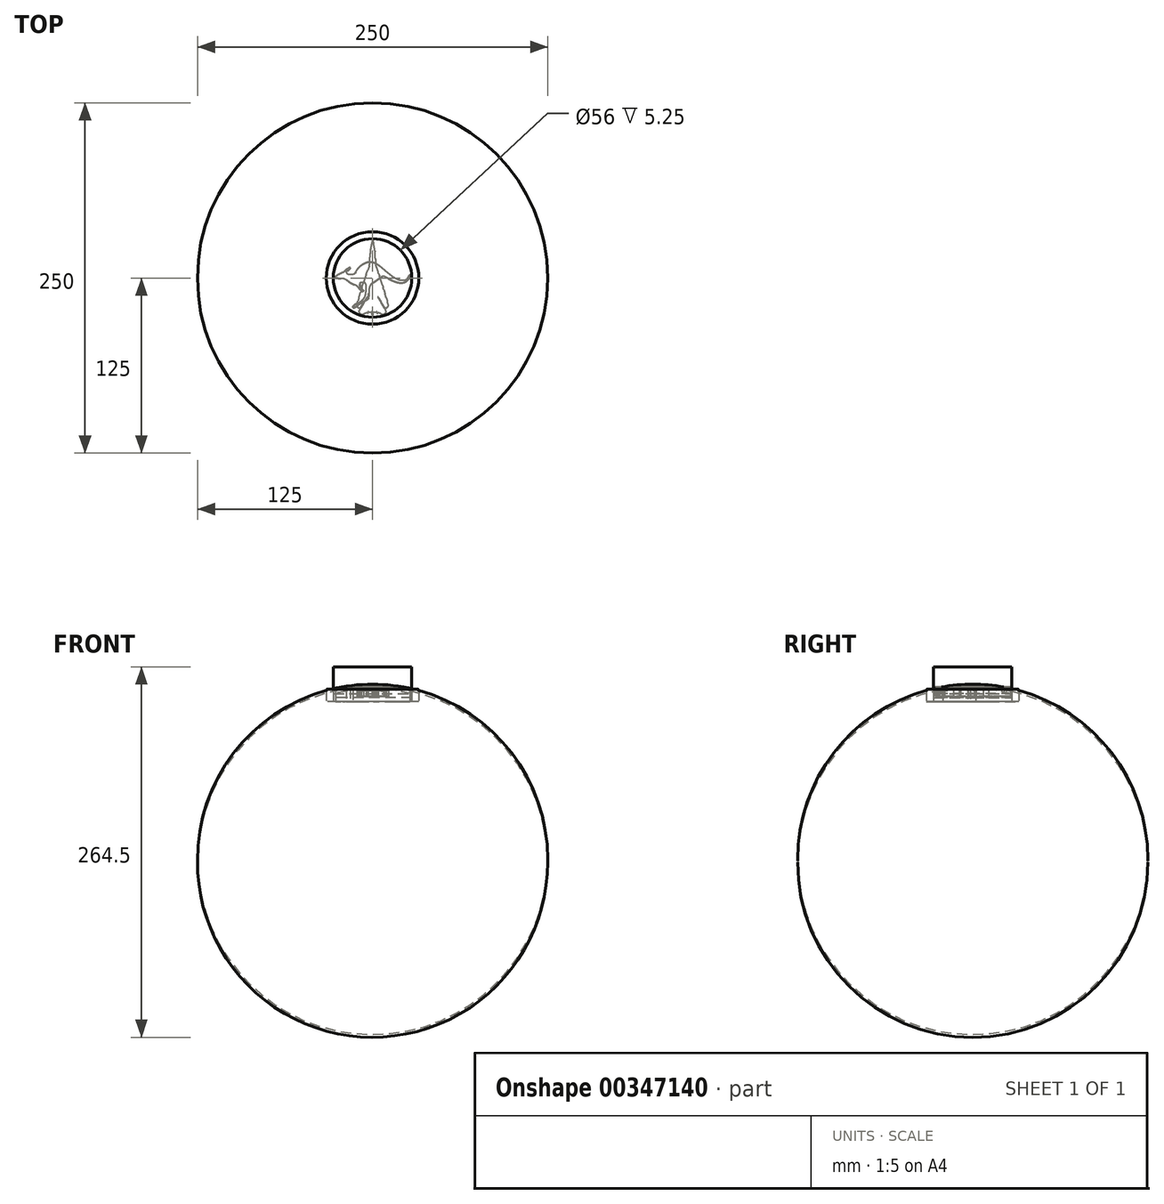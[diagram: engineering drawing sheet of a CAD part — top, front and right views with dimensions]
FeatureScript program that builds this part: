
annotation { "Feature Type Name" : "Feature", "Feature Type Description" : "" }
export const myFeature = defineFeature(function(context is Context, id is Id, definition is map)
    precondition{}
    {
        {
            var Q0;
            Q0=qCreatedBy(makeId("Top.planeOp"),FACE);
            var sketch = newSketch(context, id + "F0", { "sketchPlane" : qUnion([Q0])});
            skCircle(sketch, "E0", {"center": v(0, 0) * mm, "radius": 33 * mm});
            skSolve(sketch);
        }
        {
            var Q0;
            Q0 = qSketchRegion(id + "F0", true);
            extrude(context, id + "F1", {"entities" : qUnion([Q0]), "depth" : 3 * mm});
        }
        {
            var Q0;
            Q0=qCreatedBy(makeId("Top.planeOp"),FACE);
            var sketch = newSketch(context, id + "F2", { "sketchPlane" : qUnion([Q0])});
            skCircle(sketch, "E1", {"center": v(0, 0) * mm, "radius": 33 * mm});
            skCircle(sketch, "E2", {"center": v(0, 0) * mm, "radius": 28 * mm});
            skSolve(sketch);
        }
        {
            var Q0;
            Q0 = qSketchRegion(id + "F2", true);
            extrude(context, id + "F3", {"entities" : qUnion([Q0]), "operationType" : NewBodyOperationType.ADD, "depth" : 9 * mm});
        }
        {
            var Q0;
            Q0=makeQuery(id+"F3.opExtrude","CAP_EDGE",EDGE,{"disambiguationData":[OSD([sQuery(id+"F2.wireOp",EDGE,"E1")])],"isStart":false});
            var Q1;
            Q1=makeQuery(id+"F3.opExtrude","CAP_EDGE",EDGE,{"disambiguationData":[OSD([sQuery(id+"F2.wireOp",EDGE,"E2")])],"isStart":false});
            fillet(context, id + "F4", {"entities" : qUnion([Q0, Q1]), "radius" : 0.75 * mm, "tangentPropagation" : true, "allowEdgeOverflow" : false});
        }
        {
            var Q0;
            Q0=qCreatedBy(makeId("Top.planeOp"),FACE);
            var sketch = newSketch(context, id + "F5", { "sketchPlane" : qUnion([Q0])});
            skArc(sketch, "E3", {"start": v(0, 125) * mm, "mid": v(-125, 0) * mm, "end": v(0, -125) * mm});
            skLineSegment(sketch, "E4", {"start": v(0, 0) * mm, "end": v(0, 125) * mm});
            skLineSegment(sketch, "E5", {"start": v(0, 0) * mm, "end": v(0, -125) * mm});
            skSolve(sketch);
        }
        {
            var Q0;
            Q0=makeQuery(id+"F5.imprint","IMPRINT",FACE,{"disambiguationData":[TD([[makeQuery(id+"F5.imprint","IMPRINT",EDGE,{"derivedFrom":sQuery(id+"F5.wireOp",EDGE,"E3")}),1.0]])]});
            var Q1;
            Q1=sQuery(id+"F5.wireOp",EDGE,"E4");
            revolve(context, id + "F6", {"entities" : qUnion([Q0]), "axis" : qUnion([Q1]), "revolveType" : RevolveType.FULL});
        }
        {
            var Q0;
            Q0=makeQuery(id+"F6.opRevolve","SWEPT_BODY",BODY,{"disambiguationData":[OSD([sQuery(id+"F5.wireOp",EDGE,"E3"),sQuery(id+"F5.wireOp",EDGE,"E4"),sQuery(id+"F5.wireOp",EDGE,"E5")])]});
            transform(context, id + "F7", {"entities" : qUnion([Q0]), "transformType" : TransformType.TRANSLATION_3D, "dx" : 0 * mm, "dy" : 0 * mm, "dz" : -112.5 * mm, "makeCopy" : false});
        }
        {
            var Q0;
            Q0=qCreatedBy(makeId("Top.planeOp"),FACE);
            var sketch = newSketch(context, id + "F8", { "sketchPlane" : qUnion([Q0])});
            skArc(sketch, "E6", {"start": v(-1.06, 204.98) * mm, "mid": v(-3.06, 197.7) * mm, "end": v(-4.96, 190.37) * mm});
            skArc(sketch, "E7", {"start": v(-4.96, 190.37) * mm, "mid": v(-6.57, 183.77) * mm, "end": v(-8.05, 177.14) * mm});
            skArc(sketch, "E8", {"start": v(-8.05, 177.14) * mm, "mid": v(-9.38, 170.65) * mm, "end": v(-10.58, 164.14) * mm});
            skArc(sketch, "E9", {"start": v(-10.58, 164.14) * mm, "mid": v(-11.75, 157.2) * mm, "end": v(-12.8, 150.23) * mm});
            skArc(sketch, "E10", {"start": v(-12.8, 150.23) * mm, "mid": v(-13.03, 148.33) * mm, "end": v(-13.2, 146.42) * mm});
            skArc(sketch, "E11", {"start": v(-13.2, 146.42) * mm, "mid": v(-13.47, 141.8) * mm, "end": v(-13.73, 137.18) * mm});
            skArc(sketch, "E12", {"start": v(-13.73, 137.18) * mm, "mid": v(-14.01, 131.67) * mm, "end": v(-14.27, 126.16) * mm});
            skArc(sketch, "E13", {"start": v(-14.27, 126.16) * mm, "mid": v(-14.52, 120.2) * mm, "end": v(-14.75, 114.23) * mm});
            skArc(sketch, "E14", {"start": v(-14.75, 114.23) * mm, "mid": v(-14.97, 108.2) * mm, "end": v(-15.2, 102.16) * mm});
            skArc(sketch, "E15", {"start": v(-15.2, 102.16) * mm, "mid": v(-15.4, 96.43) * mm, "end": v(-15.62, 90.7) * mm});
            skArc(sketch, "E16", {"start": v(-15.62, 90.7) * mm, "mid": v(-15.8, 85.85) * mm, "end": v(-15.98, 81) * mm});
            skArc(sketch, "E17", {"start": v(-15.98, 81) * mm, "mid": v(-16.08, 78.62) * mm, "end": v(-16.17, 76.23) * mm});
            skArc(sketch, "E18", {"start": v(-16.17, 76.23) * mm, "mid": v(-16.27, 74.54) * mm, "end": v(-16.41, 72.86) * mm});
            skArc(sketch, "E19", {"start": v(-16.41, 72.86) * mm, "mid": v(-16.61, 71.19) * mm, "end": v(-16.86, 69.53) * mm});
            skArc(sketch, "E20", {"start": v(-16.86, 69.53) * mm, "mid": v(-17.13, 68.08) * mm, "end": v(-17.45, 66.63) * mm});
            skArc(sketch, "E21", {"start": v(-17.45, 66.63) * mm, "mid": v(-17.73, 65.67) * mm, "end": v(-18.1, 64.73) * mm});
            skArc(sketch, "E22", {"start": v(-18.1, 64.73) * mm, "mid": v(-18.6, 63.61) * mm, "end": v(-19.05, 62.47) * mm});
            skArc(sketch, "E23", {"start": v(-19.05, 62.47) * mm, "mid": v(-20.12, 59.65) * mm, "end": v(-21.18, 56.83) * mm});
            skArc(sketch, "E24", {"start": v(-21.18, 56.83) * mm, "mid": v(-22.43, 53.45) * mm, "end": v(-23.67, 50.07) * mm});
            skArc(sketch, "E25", {"start": v(-23.67, 50.07) * mm, "mid": v(-25, 46.4) * mm, "end": v(-26.32, 42.73) * mm});
            skArc(sketch, "E26", {"start": v(-26.32, 42.73) * mm, "mid": v(-27.66, 39) * mm, "end": v(-29, 35.28) * mm});
            skArc(sketch, "E27", {"start": v(-29, 35.28) * mm, "mid": v(-30.27, 31.74) * mm, "end": v(-31.55, 28.2) * mm});
            skArc(sketch, "E28", {"start": v(-31.55, 28.2) * mm, "mid": v(-32.63, 25.2) * mm, "end": v(-33.72, 22.2) * mm});
            skArc(sketch, "E29", {"start": v(-33.72, 22.2) * mm, "mid": v(-34.26, 20.72) * mm, "end": v(-34.81, 19.23) * mm});
            skArc(sketch, "E30", {"start": v(-34.81, 19.23) * mm, "mid": v(-37.05, 13.14) * mm, "end": v(-39.24, 7.03) * mm});
            skArc(sketch, "E31", {"start": v(-39.24, 7.03) * mm, "mid": v(-41.5, 0.56) * mm, "end": v(-43.7, -5.92) * mm});
            skArc(sketch, "E32", {"start": v(-43.7, -5.92) * mm, "mid": v(-45.8, -12.23) * mm, "end": v(-47.85, -18.55) * mm});
            skArc(sketch, "E33", {"start": v(-47.85, -18.55) * mm, "mid": v(-49.62, -24.15) * mm, "end": v(-51.32, -29.77) * mm});
            skArc(sketch, "E34", {"start": v(-51.32, -29.77) * mm, "mid": v(-52.3, -33.05) * mm, "end": v(-53.27, -36.33) * mm});
            skArc(sketch, "E35", {"start": v(-53.27, -36.33) * mm, "mid": v(-54.25, -39.58) * mm, "end": v(-55.22, -42.83) * mm});
            skArc(sketch, "E36", {"start": v(-55.22, -42.83) * mm, "mid": v(-56.06, -45.64) * mm, "end": v(-56.91, -48.46) * mm});
            skArc(sketch, "E37", {"start": v(-56.91, -48.46) * mm, "mid": v(-57.41, -50.11) * mm, "end": v(-57.92, -51.77) * mm});
            skArc(sketch, "E38", {"start": v(-57.92, -51.77) * mm, "mid": v(-58.46, -53.54) * mm, "end": v(-59, -55.32) * mm});
            skArc(sketch, "E39", {"start": v(-59, -55.32) * mm, "mid": v(-60.07, -58.9) * mm, "end": v(-61.14, -62.47) * mm});
            skArc(sketch, "E40", {"start": v(-61.14, -62.47) * mm, "mid": v(-62.4, -66.69) * mm, "end": v(-63.66, -70.9) * mm});
            skArc(sketch, "E41", {"start": v(-63.66, -70.9) * mm, "mid": v(-64.98, -75.34) * mm, "end": v(-66.3, -79.77) * mm});
            skArc(sketch, "E42", {"start": v(-66.3, -79.77) * mm, "mid": v(-67.61, -84.2) * mm, "end": v(-68.93, -88.63) * mm});
            skArc(sketch, "E43", {"start": v(-68.93, -88.63) * mm, "mid": v(-70.2, -92.85) * mm, "end": v(-71.46, -97.07) * mm});
            skArc(sketch, "E44", {"start": v(-71.46, -97.07) * mm, "mid": v(-72.54, -100.64) * mm, "end": v(-73.62, -104.2) * mm});
            skArc(sketch, "E45", {"start": v(-73.62, -104.2) * mm, "mid": v(-74.16, -105.99) * mm, "end": v(-74.72, -107.77) * mm});
            skArc(sketch, "E46", {"start": v(-74.72, -107.77) * mm, "mid": v(-75.2, -109.29) * mm, "end": v(-75.66, -110.82) * mm});
            skArc(sketch, "E47", {"start": v(-75.66, -110.82) * mm, "mid": v(-76.33, -113.03) * mm, "end": v(-76.99, -115.24) * mm});
            skArc(sketch, "E48", {"start": v(-76.99, -115.24) * mm, "mid": v(-77.71, -117.67) * mm, "end": v(-78.43, -120.12) * mm});
            skArc(sketch, "E49", {"start": v(-78.43, -120.12) * mm, "mid": v(-79.11, -122.44) * mm, "end": v(-79.79, -124.77) * mm});
            skArc(sketch, "E50", {"start": v(-79.79, -124.77) * mm, "mid": v(-80.44, -127.01) * mm, "end": v(-81.11, -129.26) * mm});
            skArc(sketch, "E51", {"start": v(-81.11, -129.26) * mm, "mid": v(-81.78, -131.46) * mm, "end": v(-82.46, -133.66) * mm});
            skArc(sketch, "E52", {"start": v(-82.46, -133.66) * mm, "mid": v(-83.05, -135.55) * mm, "end": v(-83.66, -137.44) * mm});
            skArc(sketch, "E53", {"start": v(-83.66, -137.44) * mm, "mid": v(-84.02, -138.52) * mm, "end": v(-84.4, -139.6) * mm});
            skArc(sketch, "E54", {"start": v(-84.4, -139.6) * mm, "mid": v(-84.73, -140.52) * mm, "end": v(-85, -141.46) * mm});
            skArc(sketch, "E55", {"start": v(-85, -141.46) * mm, "mid": v(-85.32, -142.71) * mm, "end": v(-85.6, -143.97) * mm});
            skArc(sketch, "E56", {"start": v(-85.6, -143.97) * mm, "mid": v(-85.87, -145.3) * mm, "end": v(-86.11, -146.65) * mm});
            skArc(sketch, "E57", {"start": v(-86.11, -146.65) * mm, "mid": v(-86.3, -147.88) * mm, "end": v(-86.44, -149.11) * mm});
            skLineSegment(sketch, "E58", {"start": v(-86.44, -149.11) * mm, "end": v(-87.04, -154.8) * mm});
            skLineSegment(sketch, "E59", {"start": v(-87.04, -154.8) * mm, "end": v(-82.61, -158.78) * mm});
            skArc(sketch, "E60", {"start": v(-82.61, -158.78) * mm, "mid": v(-80.32, -160.83) * mm, "end": v(-78.01, -162.85) * mm});
            skArc(sketch, "E61", {"start": v(-78.01, -162.85) * mm, "mid": v(-76.6, -164.03) * mm, "end": v(-75.15, -165.16) * mm});
            skArc(sketch, "E62", {"start": v(-75.15, -165.16) * mm, "mid": v(-74.15, -165.86) * mm, "end": v(-73.12, -166.5) * mm});
            skArc(sketch, "E63", {"start": v(-73.12, -166.5) * mm, "mid": v(-72.35, -166.85) * mm, "end": v(-71.54, -167.06) * mm});
            skArc(sketch, "E64", {"start": v(-71.54, -167.06) * mm, "mid": v(-70.52, -166.96) * mm, "end": v(-69.69, -166.35) * mm});
            skArc(sketch, "E65", {"start": v(-69.69, -166.35) * mm, "mid": v(-67.91, -164.03) * mm, "end": v(-66.22, -161.65) * mm});
            skArc(sketch, "E66", {"start": v(-66.22, -161.65) * mm, "mid": v(-63.23, -157.17) * mm, "end": v(-60.33, -152.63) * mm});
            skArc(sketch, "E67", {"start": v(-60.33, -152.63) * mm, "mid": v(-52.8, -140.6) * mm, "end": v(-45.3, -128.56) * mm});
            skArc(sketch, "E68", {"start": v(-45.3, -128.56) * mm, "mid": v(-42.19, -123.59) * mm, "end": v(-39.04, -118.63) * mm});
            skArc(sketch, "E69", {"start": v(-39.04, -118.63) * mm, "mid": v(-36.68, -115.01) * mm, "end": v(-34.26, -111.43) * mm});
            skArc(sketch, "E70", {"start": v(-34.26, -111.43) * mm, "mid": v(-32.42, -108.78) * mm, "end": v(-30.55, -106.14) * mm});
            skArc(sketch, "E71", {"start": v(-30.55, -106.14) * mm, "mid": v(-30.23, -106.02) * mm, "end": v(-30, -106.27) * mm});
            skArc(sketch, "E72", {"start": v(-30, -106.27) * mm, "mid": v(-30, -106.96) * mm, "end": v(-30.23, -107.61) * mm});
            skArc(sketch, "E73", {"start": v(-30.23, -107.61) * mm, "mid": v(-32.67, -111.88) * mm, "end": v(-35.13, -116.13) * mm});
            skArc(sketch, "E74", {"start": v(-35.13, -116.13) * mm, "mid": v(-38.05, -121.11) * mm, "end": v(-41.03, -126.07) * mm});
            skArc(sketch, "E75", {"start": v(-41.03, -126.07) * mm, "mid": v(-44.62, -131.93) * mm, "end": v(-48.24, -137.77) * mm});
            skArc(sketch, "E76", {"start": v(-48.24, -137.77) * mm, "mid": v(-51.81, -143.5) * mm, "end": v(-55.36, -149.25) * mm});
            skArc(sketch, "E77", {"start": v(-55.36, -149.25) * mm, "mid": v(-58.37, -154.2) * mm, "end": v(-61.35, -159.16) * mm});
            skArc(sketch, "E78", {"start": v(-61.35, -159.16) * mm, "mid": v(-63.93, -163.5) * mm, "end": v(-66.5, -167.85) * mm});
            skArc(sketch, "E79", {"start": v(-66.5, -167.85) * mm, "mid": v(-66.73, -168.37) * mm, "end": v(-66.8, -168.92) * mm});
            skArc(sketch, "E80", {"start": v(-66.8, -168.92) * mm, "mid": v(-66.85, -169.34) * mm, "end": v(-66.97, -169.75) * mm});
            skArc(sketch, "E81", {"start": v(-66.97, -169.75) * mm, "mid": v(-67.32, -170.5) * mm, "end": v(-67.68, -171.25) * mm});
            skArc(sketch, "E82", {"start": v(-67.68, -171.25) * mm, "mid": v(-68.15, -172.13) * mm, "end": v(-68.65, -172.99) * mm});
            skArc(sketch, "E83", {"start": v(-68.65, -172.99) * mm, "mid": v(-69.22, -173.89) * mm, "end": v(-69.8, -174.77) * mm});
            skArc(sketch, "E84", {"start": v(-69.8, -174.77) * mm, "mid": v(-70.39, -175.63) * mm, "end": v(-70.95, -176.5) * mm});
            skArc(sketch, "E85", {"start": v(-70.95, -176.5) * mm, "mid": v(-71.45, -177.3) * mm, "end": v(-71.92, -178.12) * mm});
            skArc(sketch, "E86", {"start": v(-71.92, -178.12) * mm, "mid": v(-72.3, -178.8) * mm, "end": v(-72.66, -179.5) * mm});
            skArc(sketch, "E87", {"start": v(-72.66, -179.5) * mm, "mid": v(-72.77, -179.78) * mm, "end": v(-72.8, -180.07) * mm});
            skArc(sketch, "E88", {"start": v(-72.8, -180.07) * mm, "mid": v(-72.83, -180.3) * mm, "end": v(-72.9, -180.52) * mm});
            skArc(sketch, "E89", {"start": v(-72.9, -180.52) * mm, "mid": v(-73.06, -180.82) * mm, "end": v(-73.24, -181.1) * mm});
            skArc(sketch, "E90", {"start": v(-73.24, -181.1) * mm, "mid": v(-73.47, -181.42) * mm, "end": v(-73.73, -181.72) * mm});
            skArc(sketch, "E91", {"start": v(-73.73, -181.72) * mm, "mid": v(-74, -182) * mm, "end": v(-74.3, -182.27) * mm});
            skArc(sketch, "E92", {"start": v(-74.3, -182.27) * mm, "mid": v(-75.1, -183.2) * mm, "end": v(-75.57, -184.33) * mm});
            skArc(sketch, "E93", {"start": v(-75.57, -184.33) * mm, "mid": v(-75.65, -185.57) * mm, "end": v(-75.33, -186.77) * mm});
            skArc(sketch, "E94", {"start": v(-75.33, -186.77) * mm, "mid": v(-74.44, -188.46) * mm, "end": v(-73.29, -190) * mm});
            skArc(sketch, "E95", {"start": v(-73.29, -190) * mm, "mid": v(-71.11, -192.4) * mm, "end": v(-68.86, -194.71) * mm});
            skLineSegment(sketch, "E96", {"start": v(-68.86, -194.71) * mm, "end": v(-61.91, -201.6) * mm});
            skLineSegment(sketch, "E97", {"start": v(-61.91, -201.6) * mm, "end": v(-45.75, -196.22) * mm});
            skArc(sketch, "E98", {"start": v(-45.75, -196.22) * mm, "mid": v(-40.84, -194.6) * mm, "end": v(-35.92, -193) * mm});
            skArc(sketch, "E99", {"start": v(-35.92, -193) * mm, "mid": v(-33.9, -192.4) * mm, "end": v(-31.87, -191.92) * mm});
            skArc(sketch, "E100", {"start": v(-31.87, -191.92) * mm, "mid": v(-30.77, -191.77) * mm, "end": v(-29.66, -191.8) * mm});
            skArc(sketch, "E101", {"start": v(-29.66, -191.8) * mm, "mid": v(-28.92, -192.03) * mm, "end": v(-28.34, -192.55) * mm});
            skArc(sketch, "E102", {"start": v(-28.34, -192.55) * mm, "mid": v(-28.05, -192.9) * mm, "end": v(-27.73, -193.2) * mm});
            skArc(sketch, "E103", {"start": v(-27.73, -193.2) * mm, "mid": v(-27.36, -193.5) * mm, "end": v(-26.95, -193.76) * mm});
            skArc(sketch, "E104", {"start": v(-26.95, -193.76) * mm, "mid": v(-26.55, -193.97) * mm, "end": v(-26.13, -194.14) * mm});
            skArc(sketch, "E105", {"start": v(-26.13, -194.14) * mm, "mid": v(-25.77, -194.24) * mm, "end": v(-25.4, -194.27) * mm});
            skArc(sketch, "E106", {"start": v(-25.4, -194.27) * mm, "mid": v(-24.96, -194.2) * mm, "end": v(-24.56, -194) * mm});
            skArc(sketch, "E107", {"start": v(-24.56, -194) * mm, "mid": v(-24.26, -193.7) * mm, "end": v(-24.07, -193.31) * mm});
            skArc(sketch, "E108", {"start": v(-24.07, -193.31) * mm, "mid": v(-23.92, -192.63) * mm, "end": v(-23.87, -191.94) * mm});
            skArc(sketch, "E109", {"start": v(-23.87, -191.94) * mm, "mid": v(-23.89, -190.61) * mm, "end": v(-23.93, -189.28) * mm});
            skArc(sketch, "E110", {"start": v(-23.93, -189.28) * mm, "mid": v(-23.97, -187.55) * mm, "end": v(-23.94, -185.82) * mm});
            skArc(sketch, "E111", {"start": v(-23.94, -185.82) * mm, "mid": v(-23.8, -184.8) * mm, "end": v(-23.49, -183.8) * mm});
            skArc(sketch, "E112", {"start": v(-23.49, -183.8) * mm, "mid": v(-23.19, -183.57) * mm, "end": v(-22.83, -183.7) * mm});
            skArc(sketch, "E113", {"start": v(-22.83, -183.7) * mm, "mid": v(-22.42, -184.35) * mm, "end": v(-22.15, -185.06) * mm});
            skArc(sketch, "E114", {"start": v(-22.15, -185.06) * mm, "mid": v(-21.9, -185.7) * mm, "end": v(-21.51, -186.27) * mm});
            skArc(sketch, "E115", {"start": v(-21.51, -186.27) * mm, "mid": v(-21.04, -186.68) * mm, "end": v(-20.46, -186.93) * mm});
            skArc(sketch, "E116", {"start": v(-20.46, -186.93) * mm, "mid": v(-19.48, -187.13) * mm, "end": v(-18.48, -187.2) * mm});
            skArc(sketch, "E117", {"start": v(-18.48, -187.2) * mm, "mid": v(-16.14, -187.25) * mm, "end": v(-13.8, -187.27) * mm});
            skArc(sketch, "E118", {"start": v(-13.8, -187.27) * mm, "mid": v(-11.45, -187.25) * mm, "end": v(-9.1, -187.2) * mm});
            skArc(sketch, "E119", {"start": v(-9.1, -187.2) * mm, "mid": v(-8.1, -187.13) * mm, "end": v(-7.13, -186.93) * mm});
            skArc(sketch, "E120", {"start": v(-7.13, -186.93) * mm, "mid": v(-6.56, -186.68) * mm, "end": v(-6.09, -186.26) * mm});
            skArc(sketch, "E121", {"start": v(-6.09, -186.26) * mm, "mid": v(-5.7, -185.68) * mm, "end": v(-5.45, -185.03) * mm});
            skArc(sketch, "E122", {"start": v(-5.45, -185.03) * mm, "mid": v(-5.13, -184.33) * mm, "end": v(-4.58, -183.77) * mm});
            skArc(sketch, "E123", {"start": v(-4.58, -183.77) * mm, "mid": v(-4.06, -183.67) * mm, "end": v(-3.66, -184) * mm});
            skArc(sketch, "E124", {"start": v(-3.66, -184) * mm, "mid": v(-3.2, -185.24) * mm, "end": v(-2.97, -186.54) * mm});
            skArc(sketch, "E125", {"start": v(-2.97, -186.54) * mm, "mid": v(-2.9, -188.35) * mm, "end": v(-2.95, -190.17) * mm});
            skArc(sketch, "E126", {"start": v(-2.95, -190.17) * mm, "mid": v(-3, -191.15) * mm, "end": v(-3.03, -192.13) * mm});
            skArc(sketch, "E127", {"start": v(-3.03, -192.13) * mm, "mid": v(-3.02, -192.95) * mm, "end": v(-2.98, -193.77) * mm});
            skArc(sketch, "E128", {"start": v(-2.98, -193.77) * mm, "mid": v(-2.92, -194.4) * mm, "end": v(-2.83, -195.03) * mm});
            skArc(sketch, "E129", {"start": v(-2.83, -195.03) * mm, "mid": v(-2.74, -195.2) * mm, "end": v(-2.55, -195.27) * mm});
            skArc(sketch, "E130", {"start": v(-2.55, -195.27) * mm, "mid": v(-2.36, -195.34) * mm, "end": v(-2.26, -195.5) * mm});
            skArc(sketch, "E131", {"start": v(-2.26, -195.5) * mm, "mid": v(-2.13, -196.18) * mm, "end": v(-2.02, -196.87) * mm});
            skArc(sketch, "E132", {"start": v(-2.02, -196.87) * mm, "mid": v(-1.92, -197.74) * mm, "end": v(-1.86, -198.62) * mm});
            skArc(sketch, "E133", {"start": v(-1.86, -198.62) * mm, "mid": v(-1.82, -199.66) * mm, "end": v(-1.8, -200.7) * mm});
            skArc(sketch, "E134", {"start": v(-1.8, -200.7) * mm, "mid": v(-1.76, -202.46) * mm, "end": v(-1.64, -204.2) * mm});
            skArc(sketch, "E135", {"start": v(-1.64, -204.2) * mm, "mid": v(-1.43, -205.28) * mm, "end": v(-1.04, -206.3) * mm});
            skArc(sketch, "E136", {"start": v(-1.04, -206.3) * mm, "mid": v(-0.68, -206.67) * mm, "end": v(-0.17, -206.74) * mm});
            skArc(sketch, "E137", {"start": v(-0.17, -206.74) * mm, "mid": v(0.4, -206.51) * mm, "end": v(0.82, -206.07) * mm});
            skArc(sketch, "E138", {"start": v(0.82, -206.07) * mm, "mid": v(1, -205.72) * mm, "end": v(1.1, -205.34) * mm});
            skArc(sketch, "E139", {"start": v(1.1, -205.34) * mm, "mid": v(1.2, -204.66) * mm, "end": v(1.28, -203.98) * mm});
            skArc(sketch, "E140", {"start": v(1.28, -203.98) * mm, "mid": v(1.33, -203.17) * mm, "end": v(1.36, -202.35) * mm});
            skArc(sketch, "E141", {"start": v(1.36, -202.35) * mm, "mid": v(1.35, -201.5) * mm, "end": v(1.32, -200.66) * mm});
            skArc(sketch, "E142", {"start": v(1.32, -200.66) * mm, "mid": v(1.29, -199.83) * mm, "end": v(1.3, -199) * mm});
            skArc(sketch, "E143", {"start": v(1.3, -199) * mm, "mid": v(1.35, -198.25) * mm, "end": v(1.45, -197.5) * mm});
            skArc(sketch, "E144", {"start": v(1.45, -197.5) * mm, "mid": v(1.57, -196.91) * mm, "end": v(1.73, -196.32) * mm});
            skArc(sketch, "E145", {"start": v(1.73, -196.32) * mm, "mid": v(1.88, -196.03) * mm, "end": v(2.13, -195.8) * mm});
            skArc(sketch, "E146", {"start": v(2.13, -195.8) * mm, "mid": v(2.39, -195.57) * mm, "end": v(2.55, -195.25) * mm});
            skArc(sketch, "E147", {"start": v(2.55, -195.25) * mm, "mid": v(2.73, -194.5) * mm, "end": v(2.88, -193.74) * mm});
            skArc(sketch, "E148", {"start": v(2.88, -193.74) * mm, "mid": v(3.03, -192.8) * mm, "end": v(3.12, -191.84) * mm});
            skArc(sketch, "E149", {"start": v(3.12, -191.84) * mm, "mid": v(3.18, -190.77) * mm, "end": v(3.2, -189.7) * mm});
            skArc(sketch, "E150", {"start": v(3.2, -189.7) * mm, "mid": v(3.22, -188.66) * mm, "end": v(3.27, -187.62) * mm});
            skArc(sketch, "E151", {"start": v(3.27, -187.62) * mm, "mid": v(3.36, -186.74) * mm, "end": v(3.5, -185.87) * mm});
            skArc(sketch, "E152", {"start": v(3.5, -185.87) * mm, "mid": v(3.63, -185.2) * mm, "end": v(3.8, -184.56) * mm});
            skArc(sketch, "E153", {"start": v(3.8, -184.56) * mm, "mid": v(3.95, -184.35) * mm, "end": v(4.2, -184.27) * mm});
            skArc(sketch, "E154", {"start": v(4.2, -184.27) * mm, "mid": v(4.4, -184.3) * mm, "end": v(4.58, -184.38) * mm});
            skArc(sketch, "E155", {"start": v(4.58, -184.38) * mm, "mid": v(4.76, -184.53) * mm, "end": v(4.9, -184.7) * mm});
            skArc(sketch, "E156", {"start": v(4.9, -184.7) * mm, "mid": v(5.03, -184.94) * mm, "end": v(5.12, -185.2) * mm});
            skArc(sketch, "E157", {"start": v(5.12, -185.2) * mm, "mid": v(5.18, -185.48) * mm, "end": v(5.2, -185.77) * mm});
            skArc(sketch, "E158", {"start": v(5.2, -185.77) * mm, "mid": v(5.31, -186.2) * mm, "end": v(5.63, -186.52) * mm});
            skArc(sketch, "E159", {"start": v(5.63, -186.52) * mm, "mid": v(6.23, -186.8) * mm, "end": v(6.86, -186.97) * mm});
            skArc(sketch, "E160", {"start": v(6.86, -186.97) * mm, "mid": v(8.04, -187.13) * mm, "end": v(9.22, -187.2) * mm});
            skArc(sketch, "E161", {"start": v(9.22, -187.2) * mm, "mid": v(11.46, -187.25) * mm, "end": v(13.7, -187.27) * mm});
            skArc(sketch, "E162", {"start": v(13.7, -187.27) * mm, "mid": v(15.94, -187.25) * mm, "end": v(18.18, -187.2) * mm});
            skArc(sketch, "E163", {"start": v(18.18, -187.2) * mm, "mid": v(19.36, -187.13) * mm, "end": v(20.53, -186.97) * mm});
            skArc(sketch, "E164", {"start": v(20.53, -186.97) * mm, "mid": v(21.17, -186.8) * mm, "end": v(21.77, -186.52) * mm});
            skArc(sketch, "E165", {"start": v(21.77, -186.52) * mm, "mid": v(22.08, -186.2) * mm, "end": v(22.2, -185.77) * mm});
            skArc(sketch, "E166", {"start": v(22.2, -185.77) * mm, "mid": v(22.22, -185.48) * mm, "end": v(22.27, -185.2) * mm});
            skArc(sketch, "E167", {"start": v(22.27, -185.2) * mm, "mid": v(22.36, -184.94) * mm, "end": v(22.5, -184.7) * mm});
            skArc(sketch, "E168", {"start": v(22.5, -184.7) * mm, "mid": v(22.64, -184.53) * mm, "end": v(22.82, -184.38) * mm});
            skArc(sketch, "E169", {"start": v(22.82, -184.38) * mm, "mid": v(23, -184.3) * mm, "end": v(23.2, -184.27) * mm});
            skArc(sketch, "E170", {"start": v(23.2, -184.27) * mm, "mid": v(23.44, -184.34) * mm, "end": v(23.59, -184.55) * mm});
            skArc(sketch, "E171", {"start": v(23.59, -184.55) * mm, "mid": v(23.76, -185.14) * mm, "end": v(23.9, -185.74) * mm});
            skArc(sketch, "E172", {"start": v(23.9, -185.74) * mm, "mid": v(24.04, -186.54) * mm, "end": v(24.13, -187.35) * mm});
            skArc(sketch, "E173", {"start": v(24.13, -187.35) * mm, "mid": v(24.18, -188.3) * mm, "end": v(24.2, -189.27) * mm});
            skArc(sketch, "E174", {"start": v(24.2, -189.27) * mm, "mid": v(24.21, -190.55) * mm, "end": v(24.27, -191.84) * mm});
            skArc(sketch, "E175", {"start": v(24.27, -191.84) * mm, "mid": v(24.35, -192.56) * mm, "end": v(24.53, -193.25) * mm});
            skArc(sketch, "E176", {"start": v(24.53, -193.25) * mm, "mid": v(24.73, -193.66) * mm, "end": v(25.04, -193.99) * mm});
            skArc(sketch, "E177", {"start": v(25.04, -193.99) * mm, "mid": v(25.41, -194.2) * mm, "end": v(25.84, -194.27) * mm});
            skArc(sketch, "E178", {"start": v(25.84, -194.27) * mm, "mid": v(26.2, -194.24) * mm, "end": v(26.56, -194.14) * mm});
            skArc(sketch, "E179", {"start": v(26.56, -194.14) * mm, "mid": v(26.97, -193.97) * mm, "end": v(27.36, -193.77) * mm});
            skArc(sketch, "E180", {"start": v(27.36, -193.77) * mm, "mid": v(27.76, -193.5) * mm, "end": v(28.13, -193.21) * mm});
            skArc(sketch, "E181", {"start": v(28.13, -193.21) * mm, "mid": v(28.44, -192.9) * mm, "end": v(28.72, -192.56) * mm});
            skArc(sketch, "E182", {"start": v(28.72, -192.56) * mm, "mid": v(29.3, -192.05) * mm, "end": v(30.03, -191.82) * mm});
            skArc(sketch, "E183", {"start": v(30.03, -191.82) * mm, "mid": v(31.12, -191.8) * mm, "end": v(32.2, -191.94) * mm});
            skArc(sketch, "E184", {"start": v(32.2, -191.94) * mm, "mid": v(34.2, -192.42) * mm, "end": v(36.16, -193) * mm});
            skArc(sketch, "E185", {"start": v(36.16, -193) * mm, "mid": v(40.94, -194.58) * mm, "end": v(45.7, -196.17) * mm});
            skLineSegment(sketch, "E186", {"start": v(45.7, -196.17) * mm, "end": v(61.43, -201.49) * mm});
            skLineSegment(sketch, "E187", {"start": v(61.43, -201.49) * mm, "end": v(68.81, -194.15) * mm});
            skArc(sketch, "E188", {"start": v(68.81, -194.15) * mm, "mid": v(70.24, -192.72) * mm, "end": v(71.64, -191.28) * mm});
            skArc(sketch, "E189", {"start": v(71.64, -191.28) * mm, "mid": v(72.85, -190) * mm, "end": v(74.03, -188.72) * mm});
            skArc(sketch, "E190", {"start": v(74.03, -188.72) * mm, "mid": v(75.01, -187.62) * mm, "end": v(76, -186.5) * mm});
            skArc(sketch, "E191", {"start": v(76, -186.5) * mm, "mid": v(76.14, -186.25) * mm, "end": v(76.2, -185.96) * mm});
            skArc(sketch, "E192", {"start": v(76.2, -185.96) * mm, "mid": v(76.16, -185.66) * mm, "end": v(76.05, -185.37) * mm});
            skArc(sketch, "E193", {"start": v(76.05, -185.37) * mm, "mid": v(75.4, -184.17) * mm, "end": v(74.73, -182.97) * mm});
            skArc(sketch, "E194", {"start": v(74.73, -182.97) * mm, "mid": v(73.93, -181.55) * mm, "end": v(73.11, -180.15) * mm});
            skArc(sketch, "E195", {"start": v(73.11, -180.15) * mm, "mid": v(72.16, -178.56) * mm, "end": v(71.2, -176.98) * mm});
            skArc(sketch, "E196", {"start": v(71.2, -176.98) * mm, "mid": v(70.23, -175.38) * mm, "end": v(69.28, -173.78) * mm});
            skArc(sketch, "E197", {"start": v(69.28, -173.78) * mm, "mid": v(68.46, -172.34) * mm, "end": v(67.67, -170.9) * mm});
            skArc(sketch, "E198", {"start": v(67.67, -170.9) * mm, "mid": v(67.02, -169.67) * mm, "end": v(66.38, -168.44) * mm});
            skArc(sketch, "E199", {"start": v(66.38, -168.44) * mm, "mid": v(66.24, -168.07) * mm, "end": v(66.2, -167.68) * mm});
            skArc(sketch, "E200", {"start": v(66.2, -167.68) * mm, "mid": v(66.14, -167.24) * mm, "end": v(65.96, -166.83) * mm});
            skArc(sketch, "E201", {"start": v(65.96, -166.83) * mm, "mid": v(63.45, -162.63) * mm, "end": v(60.93, -158.44) * mm});
            skArc(sketch, "E202", {"start": v(60.93, -158.44) * mm, "mid": v(58.04, -153.67) * mm, "end": v(55.13, -148.93) * mm});
            skArc(sketch, "E203", {"start": v(55.13, -148.93) * mm, "mid": v(51.7, -143.39) * mm, "end": v(48.26, -137.86) * mm});
            skArc(sketch, "E204", {"start": v(48.26, -137.86) * mm, "mid": v(44.79, -132.3) * mm, "end": v(41.34, -126.74) * mm});
            skArc(sketch, "E205", {"start": v(41.34, -126.74) * mm, "mid": v(38.36, -121.92) * mm, "end": v(35.4, -117.07) * mm});
            skArc(sketch, "E206", {"start": v(35.4, -117.07) * mm, "mid": v(32.87, -112.88) * mm, "end": v(30.33, -108.68) * mm});
            skArc(sketch, "E207", {"start": v(30.33, -108.68) * mm, "mid": v(29.98, -108.02) * mm, "end": v(29.72, -107.32) * mm});
            skArc(sketch, "E208", {"start": v(29.72, -107.32) * mm, "mid": v(29.62, -106.94) * mm, "end": v(29.56, -106.55) * mm});
            skArc(sketch, "E209", {"start": v(29.56, -106.55) * mm, "mid": v(29.56, -106.18) * mm, "end": v(29.6, -105.8) * mm});
            skArc(sketch, "E210", {"start": v(29.6, -105.8) * mm, "mid": v(29.68, -105.48) * mm, "end": v(29.8, -105.18) * mm});
            skArc(sketch, "E211", {"start": v(29.8, -105.18) * mm, "mid": v(29.95, -104.96) * mm, "end": v(30.16, -104.8) * mm});
            skArc(sketch, "E212", {"start": v(30.16, -104.8) * mm, "mid": v(30.35, -104.7) * mm, "end": v(30.55, -104.63) * mm});
            skArc(sketch, "E213", {"start": v(30.55, -104.63) * mm, "mid": v(30.73, -104.61) * mm, "end": v(30.9, -104.65) * mm});
            skArc(sketch, "E214", {"start": v(30.9, -104.65) * mm, "mid": v(31.02, -104.73) * mm, "end": v(31.12, -104.86) * mm});
            skArc(sketch, "E215", {"start": v(31.12, -104.86) * mm, "mid": v(31.18, -105.03) * mm, "end": v(31.2, -105.21) * mm});
            skArc(sketch, "E216", {"start": v(31.2, -105.21) * mm, "mid": v(31.25, -105.61) * mm, "end": v(31.41, -105.98) * mm});
            skArc(sketch, "E217", {"start": v(31.41, -105.98) * mm, "mid": v(33.45, -109.39) * mm, "end": v(35.5, -112.8) * mm});
            skArc(sketch, "E218", {"start": v(35.5, -112.8) * mm, "mid": v(37.84, -116.67) * mm, "end": v(40.21, -120.53) * mm});
            skArc(sketch, "E219", {"start": v(40.21, -120.53) * mm, "mid": v(43, -125.03) * mm, "end": v(45.82, -129.52) * mm});
            skArc(sketch, "E220", {"start": v(45.82, -129.52) * mm, "mid": v(48.78, -134.24) * mm, "end": v(51.75, -138.95) * mm});
            skArc(sketch, "E221", {"start": v(51.75, -138.95) * mm, "mid": v(54.62, -143.51) * mm, "end": v(57.48, -148.07) * mm});
            skArc(sketch, "E222", {"start": v(57.48, -148.07) * mm, "mid": v(59.93, -151.96) * mm, "end": v(62.37, -155.85) * mm});
            skArc(sketch, "E223", {"start": v(62.37, -155.85) * mm, "mid": v(63.68, -157.93) * mm, "end": v(65, -160.02) * mm});
            skArc(sketch, "E224", {"start": v(65, -160.02) * mm, "mid": v(65.9, -161.42) * mm, "end": v(66.84, -162.8) * mm});
            skArc(sketch, "E225", {"start": v(66.84, -162.8) * mm, "mid": v(67.71, -163.98) * mm, "end": v(68.63, -165.14) * mm});
            skArc(sketch, "E226", {"start": v(68.63, -165.14) * mm, "mid": v(69.4, -166.05) * mm, "end": v(70.2, -166.93) * mm});
            skArc(sketch, "E227", {"start": v(70.2, -166.93) * mm, "mid": v(70.56, -167.18) * mm, "end": v(70.98, -167.27) * mm});
            skArc(sketch, "E228", {"start": v(70.98, -167.27) * mm, "mid": v(71.8, -167.15) * mm, "end": v(72.54, -166.82) * mm});
            skArc(sketch, "E229", {"start": v(72.54, -166.82) * mm, "mid": v(73.98, -165.87) * mm, "end": v(75.38, -164.87) * mm});
            skArc(sketch, "E230", {"start": v(75.38, -164.87) * mm, "mid": v(77.2, -163.47) * mm, "end": v(78.96, -162) * mm});
            skArc(sketch, "E231", {"start": v(78.96, -162) * mm, "mid": v(81.14, -160.09) * mm, "end": v(83.28, -158.13) * mm});
            skArc(sketch, "E232", {"start": v(83.28, -158.13) * mm, "mid": v(84.88, -156.4) * mm, "end": v(86.2, -154.46) * mm});
            skArc(sketch, "E233", {"start": v(86.2, -154.46) * mm, "mid": v(86.88, -152.73) * mm, "end": v(87.02, -150.88) * mm});
            skArc(sketch, "E234", {"start": v(87.02, -150.88) * mm, "mid": v(86.66, -148.03) * mm, "end": v(86, -145.23) * mm});
            skArc(sketch, "E235", {"start": v(86, -145.23) * mm, "mid": v(83.57, -137) * mm, "end": v(81.1, -128.77) * mm});
            skArc(sketch, "E236", {"start": v(81.1, -128.77) * mm, "mid": v(80.26, -126.04) * mm, "end": v(79.43, -123.31) * mm});
            skArc(sketch, "E237", {"start": v(79.43, -123.31) * mm, "mid": v(78.58, -120.5) * mm, "end": v(77.73, -117.68) * mm});
            skArc(sketch, "E238", {"start": v(77.73, -117.68) * mm, "mid": v(76.96, -115.15) * mm, "end": v(76.2, -112.63) * mm});
            skArc(sketch, "E239", {"start": v(76.2, -112.63) * mm, "mid": v(75.7, -110.95) * mm, "end": v(75.2, -109.27) * mm});
            skArc(sketch, "E240", {"start": v(75.2, -109.27) * mm, "mid": v(74.69, -107.53) * mm, "end": v(74.17, -105.8) * mm});
            skArc(sketch, "E241", {"start": v(74.17, -105.8) * mm, "mid": v(73.34, -103.03) * mm, "end": v(72.5, -100.27) * mm});
            skArc(sketch, "E242", {"start": v(72.5, -100.27) * mm, "mid": v(71.56, -97.13) * mm, "end": v(70.6, -93.99) * mm});
            skArc(sketch, "E243", {"start": v(70.6, -93.99) * mm, "mid": v(69.67, -90.88) * mm, "end": v(68.72, -87.77) * mm});
            skArc(sketch, "E244", {"start": v(68.72, -87.77) * mm, "mid": v(67.77, -84.64) * mm, "end": v(66.83, -81.51) * mm});
            skArc(sketch, "E245", {"start": v(66.83, -81.51) * mm, "mid": v(65.86, -78.31) * mm, "end": v(64.9, -75.12) * mm});
            skArc(sketch, "E246", {"start": v(64.9, -75.12) * mm, "mid": v(64.04, -72.28) * mm, "end": v(63.18, -69.44) * mm});
            skArc(sketch, "E247", {"start": v(63.18, -69.44) * mm, "mid": v(62.63, -67.6) * mm, "end": v(62.08, -65.77) * mm});
            skArc(sketch, "E248", {"start": v(62.08, -65.77) * mm, "mid": v(61.62, -64.2) * mm, "end": v(61.15, -62.65) * mm});
            skArc(sketch, "E249", {"start": v(61.15, -62.65) * mm, "mid": v(60.62, -60.86) * mm, "end": v(60.08, -59.06) * mm});
            skArc(sketch, "E250", {"start": v(60.08, -59.06) * mm, "mid": v(59.56, -57.31) * mm, "end": v(59.04, -55.57) * mm});
            skArc(sketch, "E251", {"start": v(59.04, -55.57) * mm, "mid": v(58.62, -54.17) * mm, "end": v(58.2, -52.77) * mm});
            skArc(sketch, "E252", {"start": v(58.2, -52.77) * mm, "mid": v(57.76, -51.32) * mm, "end": v(57.33, -49.87) * mm});
            skArc(sketch, "E253", {"start": v(57.33, -49.87) * mm, "mid": v(56.76, -47.95) * mm, "end": v(56.18, -46.03) * mm});
            skArc(sketch, "E254", {"start": v(56.18, -46.03) * mm, "mid": v(55.57, -44) * mm, "end": v(54.97, -41.96) * mm});
            skArc(sketch, "E255", {"start": v(54.97, -41.96) * mm, "mid": v(54.41, -40.11) * mm, "end": v(53.86, -38.27) * mm});
            skArc(sketch, "E256", {"start": v(53.86, -38.27) * mm, "mid": v(52.05, -32.28) * mm, "end": v(50.2, -26.31) * mm});
            skArc(sketch, "E257", {"start": v(50.2, -26.31) * mm, "mid": v(47.9, -19.06) * mm, "end": v(45.56, -11.8) * mm});
            skArc(sketch, "E258", {"start": v(45.56, -11.8) * mm, "mid": v(43.32, -4.95) * mm, "end": v(41.05, 1.9) * mm});
            skArc(sketch, "E259", {"start": v(41.05, 1.9) * mm, "mid": v(39.62, 6.08) * mm, "end": v(38.12, 10.23) * mm});
            skArc(sketch, "E260", {"start": v(38.12, 10.23) * mm, "mid": v(37.47, 11.98) * mm, "end": v(36.83, 13.73) * mm});
            skArc(sketch, "E261", {"start": v(36.83, 13.73) * mm, "mid": v(36.12, 15.69) * mm, "end": v(35.41, 17.65) * mm});
            skArc(sketch, "E262", {"start": v(35.41, 17.65) * mm, "mid": v(34.74, 19.5) * mm, "end": v(34.07, 21.37) * mm});
            skArc(sketch, "E263", {"start": v(34.07, 21.37) * mm, "mid": v(33.56, 22.8) * mm, "end": v(33.06, 24.23) * mm});
            skArc(sketch, "E264", {"start": v(33.06, 24.23) * mm, "mid": v(32.61, 25.5) * mm, "end": v(32.16, 26.75) * mm});
            skArc(sketch, "E265", {"start": v(32.16, 26.75) * mm, "mid": v(31.69, 28.05) * mm, "end": v(31.2, 29.35) * mm});
            skArc(sketch, "E266", {"start": v(31.2, 29.35) * mm, "mid": v(30.77, 30.52) * mm, "end": v(30.32, 31.68) * mm});
            skArc(sketch, "E267", {"start": v(30.32, 31.68) * mm, "mid": v(30.01, 32.46) * mm, "end": v(29.7, 33.23) * mm});
            skArc(sketch, "E268", {"start": v(29.7, 33.23) * mm, "mid": v(28.92, 35.14) * mm, "end": v(28.18, 37.07) * mm});
            skArc(sketch, "E269", {"start": v(28.18, 37.07) * mm, "mid": v(26.12, 42.7) * mm, "end": v(24.06, 48.32) * mm});
            skArc(sketch, "E270", {"start": v(24.06, 48.32) * mm, "mid": v(22.04, 53.88) * mm, "end": v(20.03, 59.45) * mm});
            skArc(sketch, "E271", {"start": v(20.03, 59.45) * mm, "mid": v(18.83, 62.83) * mm, "end": v(17.66, 66.23) * mm});
            skArc(sketch, "E272", {"start": v(17.66, 66.23) * mm, "mid": v(17.2, 67.9) * mm, "end": v(16.97, 69.6) * mm});
            skArc(sketch, "E273", {"start": v(16.97, 69.6) * mm, "mid": v(16.64, 73.91) * mm, "end": v(16.37, 78.22) * mm});
            skArc(sketch, "E274", {"start": v(16.37, 78.22) * mm, "mid": v(16.05, 84.32) * mm, "end": v(15.8, 90.43) * mm});
            skArc(sketch, "E275", {"start": v(15.8, 90.43) * mm, "mid": v(15.5, 99.33) * mm, "end": v(15.22, 108.23) * mm});
            skArc(sketch, "E276", {"start": v(15.22, 108.23) * mm, "mid": v(14.99, 115.98) * mm, "end": v(14.72, 123.73) * mm});
            skArc(sketch, "E277", {"start": v(14.72, 123.73) * mm, "mid": v(14.47, 129.8) * mm, "end": v(14.17, 135.85) * mm});
            skArc(sketch, "E278", {"start": v(14.17, 135.85) * mm, "mid": v(13.9, 140.92) * mm, "end": v(13.61, 145.98) * mm});
            skArc(sketch, "E279", {"start": v(13.61, 145.98) * mm, "mid": v(13.48, 146.34) * mm, "end": v(13.17, 146.57) * mm});
            skArc(sketch, "E280", {"start": v(13.17, 146.57) * mm, "mid": v(12.94, 146.7) * mm, "end": v(12.8, 146.94) * mm});
            skArc(sketch, "E281", {"start": v(12.8, 146.94) * mm, "mid": v(12.62, 147.47) * mm, "end": v(12.48, 148) * mm});
            skArc(sketch, "E282", {"start": v(12.48, 148) * mm, "mid": v(12.35, 148.7) * mm, "end": v(12.27, 149.41) * mm});
            skArc(sketch, "E283", {"start": v(12.27, 149.41) * mm, "mid": v(12.22, 150.2) * mm, "end": v(12.2, 151) * mm});
            skArc(sketch, "E284", {"start": v(12.2, 151) * mm, "mid": v(12.1, 154.03) * mm, "end": v(11.77, 157.04) * mm});
            skArc(sketch, "E285", {"start": v(11.77, 157.04) * mm, "mid": v(11.06, 161.7) * mm, "end": v(10.26, 166.35) * mm});
            skArc(sketch, "E286", {"start": v(10.26, 166.35) * mm, "mid": v(9.19, 171.95) * mm, "end": v(8, 177.53) * mm});
            skArc(sketch, "E287", {"start": v(8, 177.53) * mm, "mid": v(6.6, 183.72) * mm, "end": v(5.1, 189.9) * mm});
            skArc(sketch, "E288", {"start": v(5.1, 189.9) * mm, "mid": v(4.35, 192.92) * mm, "end": v(3.6, 195.94) * mm});
            skArc(sketch, "E289", {"start": v(3.6, 195.94) * mm, "mid": v(2.97, 198.54) * mm, "end": v(2.34, 201.13) * mm});
            skArc(sketch, "E290", {"start": v(2.34, 201.13) * mm, "mid": v(1.8, 203.41) * mm, "end": v(1.25, 205.7) * mm});
            skArc(sketch, "E291", {"start": v(1.25, 205.7) * mm, "mid": v(1.21, 205.92) * mm, "end": v(1.2, 206.15) * mm});
            skArc(sketch, "E292", {"start": v(1.2, 206.15) * mm, "mid": v(1.11, 206.45) * mm, "end": v(0.88, 206.67) * mm});
            skArc(sketch, "E293", {"start": v(0.88, 206.67) * mm, "mid": v(0.56, 206.76) * mm, "end": v(0.24, 206.68) * mm});
            skArc(sketch, "E294", {"start": v(0.24, 206.68) * mm, "mid": v(-0.2, 206.39) * mm, "end": v(-0.56, 206) * mm});
            skArc(sketch, "E295", {"start": v(-0.56, 206) * mm, "mid": v(-0.86, 205.51) * mm, "end": v(-1.06, 204.98) * mm});
            skSolve(sketch);
        }
        {
            var Q0;
            Q0 = qSketchRegion(id + "F8", true);
            extrude(context, id + "F9", {"entities" : qUnion([Q0]), "depth" : 50 * mm});
        }
        {
            var Q0;
            Q0=makeQuery(id+"F9.opExtrude","SWEPT_BODY",BODY,{"disambiguationData":[OSD([sQuery(id+"F8.wireOp",EDGE,"E6"),sQuery(id+"F8.wireOp",EDGE,"E7"),sQuery(id+"F8.wireOp",EDGE,"E8"),sQuery(id+"F8.wireOp",EDGE,"E9"),sQuery(id+"F8.wireOp",EDGE,"E10"),sQuery(id+"F8.wireOp",EDGE,"E11"),sQuery(id+"F8.wireOp",EDGE,"E12"),sQuery(id+"F8.wireOp",EDGE,"E13"),sQuery(id+"F8.wireOp",EDGE,"E14"),sQuery(id+"F8.wireOp",EDGE,"E15"),sQuery(id+"F8.wireOp",EDGE,"E16"),sQuery(id+"F8.wireOp",EDGE,"E17"),sQuery(id+"F8.wireOp",EDGE,"E18"),sQuery(id+"F8.wireOp",EDGE,"E19"),sQuery(id+"F8.wireOp",EDGE,"E20"),sQuery(id+"F8.wireOp",EDGE,"E21"),sQuery(id+"F8.wireOp",EDGE,"E22"),sQuery(id+"F8.wireOp",EDGE,"E23"),sQuery(id+"F8.wireOp",EDGE,"E24"),sQuery(id+"F8.wireOp",EDGE,"E25"),sQuery(id+"F8.wireOp",EDGE,"E26"),sQuery(id+"F8.wireOp",EDGE,"E27"),sQuery(id+"F8.wireOp",EDGE,"E28"),sQuery(id+"F8.wireOp",EDGE,"E29"),sQuery(id+"F8.wireOp",EDGE,"E30"),sQuery(id+"F8.wireOp",EDGE,"E31"),sQuery(id+"F8.wireOp",EDGE,"E32"),sQuery(id+"F8.wireOp",EDGE,"E33"),sQuery(id+"F8.wireOp",EDGE,"E34"),sQuery(id+"F8.wireOp",EDGE,"E35"),sQuery(id+"F8.wireOp",EDGE,"E36"),sQuery(id+"F8.wireOp",EDGE,"E37"),sQuery(id+"F8.wireOp",EDGE,"E38"),sQuery(id+"F8.wireOp",EDGE,"E39"),sQuery(id+"F8.wireOp",EDGE,"E40"),sQuery(id+"F8.wireOp",EDGE,"E41"),sQuery(id+"F8.wireOp",EDGE,"E42"),sQuery(id+"F8.wireOp",EDGE,"E43"),sQuery(id+"F8.wireOp",EDGE,"E44"),sQuery(id+"F8.wireOp",EDGE,"E45"),sQuery(id+"F8.wireOp",EDGE,"E46"),sQuery(id+"F8.wireOp",EDGE,"E47"),sQuery(id+"F8.wireOp",EDGE,"E48"),sQuery(id+"F8.wireOp",EDGE,"E49"),sQuery(id+"F8.wireOp",EDGE,"E50"),sQuery(id+"F8.wireOp",EDGE,"E51"),sQuery(id+"F8.wireOp",EDGE,"E52"),sQuery(id+"F8.wireOp",EDGE,"E53"),sQuery(id+"F8.wireOp",EDGE,"E54"),sQuery(id+"F8.wireOp",EDGE,"E55"),sQuery(id+"F8.wireOp",EDGE,"E56"),sQuery(id+"F8.wireOp",EDGE,"E57"),sQuery(id+"F8.wireOp",EDGE,"E58"),sQuery(id+"F8.wireOp",EDGE,"E59"),sQuery(id+"F8.wireOp",EDGE,"E60"),sQuery(id+"F8.wireOp",EDGE,"E61"),sQuery(id+"F8.wireOp",EDGE,"E62"),sQuery(id+"F8.wireOp",EDGE,"E63"),sQuery(id+"F8.wireOp",EDGE,"E64"),sQuery(id+"F8.wireOp",EDGE,"E65"),sQuery(id+"F8.wireOp",EDGE,"E66"),sQuery(id+"F8.wireOp",EDGE,"E67"),sQuery(id+"F8.wireOp",EDGE,"E68"),sQuery(id+"F8.wireOp",EDGE,"E69"),sQuery(id+"F8.wireOp",EDGE,"E70"),sQuery(id+"F8.wireOp",EDGE,"E71"),sQuery(id+"F8.wireOp",EDGE,"E72"),sQuery(id+"F8.wireOp",EDGE,"E73"),sQuery(id+"F8.wireOp",EDGE,"E74"),sQuery(id+"F8.wireOp",EDGE,"E75"),sQuery(id+"F8.wireOp",EDGE,"E76"),sQuery(id+"F8.wireOp",EDGE,"E77"),sQuery(id+"F8.wireOp",EDGE,"E78"),sQuery(id+"F8.wireOp",EDGE,"E79"),sQuery(id+"F8.wireOp",EDGE,"E80"),sQuery(id+"F8.wireOp",EDGE,"E81"),sQuery(id+"F8.wireOp",EDGE,"E82"),sQuery(id+"F8.wireOp",EDGE,"E83"),sQuery(id+"F8.wireOp",EDGE,"E84"),sQuery(id+"F8.wireOp",EDGE,"E85"),sQuery(id+"F8.wireOp",EDGE,"E86"),sQuery(id+"F8.wireOp",EDGE,"E87"),sQuery(id+"F8.wireOp",EDGE,"E88"),sQuery(id+"F8.wireOp",EDGE,"E89"),sQuery(id+"F8.wireOp",EDGE,"E90"),sQuery(id+"F8.wireOp",EDGE,"E91"),sQuery(id+"F8.wireOp",EDGE,"E92"),sQuery(id+"F8.wireOp",EDGE,"E93"),sQuery(id+"F8.wireOp",EDGE,"E94"),sQuery(id+"F8.wireOp",EDGE,"E95"),sQuery(id+"F8.wireOp",EDGE,"E96"),sQuery(id+"F8.wireOp",EDGE,"E97"),sQuery(id+"F8.wireOp",EDGE,"E98"),sQuery(id+"F8.wireOp",EDGE,"E99"),sQuery(id+"F8.wireOp",EDGE,"E100"),sQuery(id+"F8.wireOp",EDGE,"E101"),sQuery(id+"F8.wireOp",EDGE,"E102"),sQuery(id+"F8.wireOp",EDGE,"E103"),sQuery(id+"F8.wireOp",EDGE,"E104"),sQuery(id+"F8.wireOp",EDGE,"E105"),sQuery(id+"F8.wireOp",EDGE,"E106"),sQuery(id+"F8.wireOp",EDGE,"E107"),sQuery(id+"F8.wireOp",EDGE,"E108"),sQuery(id+"F8.wireOp",EDGE,"E109"),sQuery(id+"F8.wireOp",EDGE,"E110"),sQuery(id+"F8.wireOp",EDGE,"E111"),sQuery(id+"F8.wireOp",EDGE,"E112"),sQuery(id+"F8.wireOp",EDGE,"E113"),sQuery(id+"F8.wireOp",EDGE,"E114"),sQuery(id+"F8.wireOp",EDGE,"E115"),sQuery(id+"F8.wireOp",EDGE,"E116"),sQuery(id+"F8.wireOp",EDGE,"E117"),sQuery(id+"F8.wireOp",EDGE,"E118"),sQuery(id+"F8.wireOp",EDGE,"E119"),sQuery(id+"F8.wireOp",EDGE,"E120"),sQuery(id+"F8.wireOp",EDGE,"E121"),sQuery(id+"F8.wireOp",EDGE,"E122"),sQuery(id+"F8.wireOp",EDGE,"E123"),sQuery(id+"F8.wireOp",EDGE,"E124"),sQuery(id+"F8.wireOp",EDGE,"E125"),sQuery(id+"F8.wireOp",EDGE,"E126"),sQuery(id+"F8.wireOp",EDGE,"E127"),sQuery(id+"F8.wireOp",EDGE,"E128"),sQuery(id+"F8.wireOp",EDGE,"E129"),sQuery(id+"F8.wireOp",EDGE,"E130"),sQuery(id+"F8.wireOp",EDGE,"E131"),sQuery(id+"F8.wireOp",EDGE,"E132"),sQuery(id+"F8.wireOp",EDGE,"E133"),sQuery(id+"F8.wireOp",EDGE,"E134"),sQuery(id+"F8.wireOp",EDGE,"E135"),sQuery(id+"F8.wireOp",EDGE,"E136"),sQuery(id+"F8.wireOp",EDGE,"E137"),sQuery(id+"F8.wireOp",EDGE,"E138"),sQuery(id+"F8.wireOp",EDGE,"E139"),sQuery(id+"F8.wireOp",EDGE,"E140"),sQuery(id+"F8.wireOp",EDGE,"E141"),sQuery(id+"F8.wireOp",EDGE,"E142"),sQuery(id+"F8.wireOp",EDGE,"E143"),sQuery(id+"F8.wireOp",EDGE,"E144"),sQuery(id+"F8.wireOp",EDGE,"E145"),sQuery(id+"F8.wireOp",EDGE,"E146"),sQuery(id+"F8.wireOp",EDGE,"E147"),sQuery(id+"F8.wireOp",EDGE,"E148"),sQuery(id+"F8.wireOp",EDGE,"E149"),sQuery(id+"F8.wireOp",EDGE,"E150"),sQuery(id+"F8.wireOp",EDGE,"E151"),sQuery(id+"F8.wireOp",EDGE,"E152"),sQuery(id+"F8.wireOp",EDGE,"E153"),sQuery(id+"F8.wireOp",EDGE,"E154"),sQuery(id+"F8.wireOp",EDGE,"E155"),sQuery(id+"F8.wireOp",EDGE,"E156"),sQuery(id+"F8.wireOp",EDGE,"E157"),sQuery(id+"F8.wireOp",EDGE,"E158"),sQuery(id+"F8.wireOp",EDGE,"E159"),sQuery(id+"F8.wireOp",EDGE,"E160"),sQuery(id+"F8.wireOp",EDGE,"E161"),sQuery(id+"F8.wireOp",EDGE,"E162"),sQuery(id+"F8.wireOp",EDGE,"E163"),sQuery(id+"F8.wireOp",EDGE,"E164"),sQuery(id+"F8.wireOp",EDGE,"E165"),sQuery(id+"F8.wireOp",EDGE,"E166"),sQuery(id+"F8.wireOp",EDGE,"E167"),sQuery(id+"F8.wireOp",EDGE,"E168"),sQuery(id+"F8.wireOp",EDGE,"E169"),sQuery(id+"F8.wireOp",EDGE,"E170"),sQuery(id+"F8.wireOp",EDGE,"E171"),sQuery(id+"F8.wireOp",EDGE,"E172"),sQuery(id+"F8.wireOp",EDGE,"E173"),sQuery(id+"F8.wireOp",EDGE,"E174"),sQuery(id+"F8.wireOp",EDGE,"E175"),sQuery(id+"F8.wireOp",EDGE,"E176"),sQuery(id+"F8.wireOp",EDGE,"E177"),sQuery(id+"F8.wireOp",EDGE,"E178"),sQuery(id+"F8.wireOp",EDGE,"E179"),sQuery(id+"F8.wireOp",EDGE,"E180"),sQuery(id+"F8.wireOp",EDGE,"E181"),sQuery(id+"F8.wireOp",EDGE,"E182"),sQuery(id+"F8.wireOp",EDGE,"E183"),sQuery(id+"F8.wireOp",EDGE,"E184"),sQuery(id+"F8.wireOp",EDGE,"E185"),sQuery(id+"F8.wireOp",EDGE,"E186"),sQuery(id+"F8.wireOp",EDGE,"E187"),sQuery(id+"F8.wireOp",EDGE,"E188"),sQuery(id+"F8.wireOp",EDGE,"E189"),sQuery(id+"F8.wireOp",EDGE,"E190"),sQuery(id+"F8.wireOp",EDGE,"E191"),sQuery(id+"F8.wireOp",EDGE,"E192"),sQuery(id+"F8.wireOp",EDGE,"E193"),sQuery(id+"F8.wireOp",EDGE,"E194"),sQuery(id+"F8.wireOp",EDGE,"E195"),sQuery(id+"F8.wireOp",EDGE,"E196"),sQuery(id+"F8.wireOp",EDGE,"E197"),sQuery(id+"F8.wireOp",EDGE,"E198"),sQuery(id+"F8.wireOp",EDGE,"E199"),sQuery(id+"F8.wireOp",EDGE,"E200"),sQuery(id+"F8.wireOp",EDGE,"E201"),sQuery(id+"F8.wireOp",EDGE,"E202"),sQuery(id+"F8.wireOp",EDGE,"E203"),sQuery(id+"F8.wireOp",EDGE,"E204"),sQuery(id+"F8.wireOp",EDGE,"E205"),sQuery(id+"F8.wireOp",EDGE,"E206"),sQuery(id+"F8.wireOp",EDGE,"E207"),sQuery(id+"F8.wireOp",EDGE,"E208"),sQuery(id+"F8.wireOp",EDGE,"E209"),sQuery(id+"F8.wireOp",EDGE,"E210"),sQuery(id+"F8.wireOp",EDGE,"E211"),sQuery(id+"F8.wireOp",EDGE,"E212"),sQuery(id+"F8.wireOp",EDGE,"E213"),sQuery(id+"F8.wireOp",EDGE,"E214"),sQuery(id+"F8.wireOp",EDGE,"E215"),sQuery(id+"F8.wireOp",EDGE,"E216"),sQuery(id+"F8.wireOp",EDGE,"E217"),sQuery(id+"F8.wireOp",EDGE,"E218"),sQuery(id+"F8.wireOp",EDGE,"E219"),sQuery(id+"F8.wireOp",EDGE,"E220"),sQuery(id+"F8.wireOp",EDGE,"E221"),sQuery(id+"F8.wireOp",EDGE,"E222"),sQuery(id+"F8.wireOp",EDGE,"E223"),sQuery(id+"F8.wireOp",EDGE,"E224"),sQuery(id+"F8.wireOp",EDGE,"E225"),sQuery(id+"F8.wireOp",EDGE,"E226"),sQuery(id+"F8.wireOp",EDGE,"E227"),sQuery(id+"F8.wireOp",EDGE,"E228"),sQuery(id+"F8.wireOp",EDGE,"E229"),sQuery(id+"F8.wireOp",EDGE,"E230"),sQuery(id+"F8.wireOp",EDGE,"E231"),sQuery(id+"F8.wireOp",EDGE,"E232"),sQuery(id+"F8.wireOp",EDGE,"E233"),sQuery(id+"F8.wireOp",EDGE,"E234"),sQuery(id+"F8.wireOp",EDGE,"E235"),sQuery(id+"F8.wireOp",EDGE,"E236"),sQuery(id+"F8.wireOp",EDGE,"E237"),sQuery(id+"F8.wireOp",EDGE,"E238"),sQuery(id+"F8.wireOp",EDGE,"E239"),sQuery(id+"F8.wireOp",EDGE,"E240"),sQuery(id+"F8.wireOp",EDGE,"E241"),sQuery(id+"F8.wireOp",EDGE,"E242"),sQuery(id+"F8.wireOp",EDGE,"E243"),sQuery(id+"F8.wireOp",EDGE,"E244"),sQuery(id+"F8.wireOp",EDGE,"E245"),sQuery(id+"F8.wireOp",EDGE,"E246"),sQuery(id+"F8.wireOp",EDGE,"E247"),sQuery(id+"F8.wireOp",EDGE,"E248"),sQuery(id+"F8.wireOp",EDGE,"E249"),sQuery(id+"F8.wireOp",EDGE,"E250"),sQuery(id+"F8.wireOp",EDGE,"E251"),sQuery(id+"F8.wireOp",EDGE,"E252"),sQuery(id+"F8.wireOp",EDGE,"E253"),sQuery(id+"F8.wireOp",EDGE,"E254"),sQuery(id+"F8.wireOp",EDGE,"E255"),sQuery(id+"F8.wireOp",EDGE,"E256"),sQuery(id+"F8.wireOp",EDGE,"E257"),sQuery(id+"F8.wireOp",EDGE,"E258"),sQuery(id+"F8.wireOp",EDGE,"E259"),sQuery(id+"F8.wireOp",EDGE,"E260"),sQuery(id+"F8.wireOp",EDGE,"E261"),sQuery(id+"F8.wireOp",EDGE,"E262"),sQuery(id+"F8.wireOp",EDGE,"E263"),sQuery(id+"F8.wireOp",EDGE,"E264"),sQuery(id+"F8.wireOp",EDGE,"E265"),sQuery(id+"F8.wireOp",EDGE,"E266"),sQuery(id+"F8.wireOp",EDGE,"E267"),sQuery(id+"F8.wireOp",EDGE,"E268"),sQuery(id+"F8.wireOp",EDGE,"E269"),sQuery(id+"F8.wireOp",EDGE,"E270"),sQuery(id+"F8.wireOp",EDGE,"E271"),sQuery(id+"F8.wireOp",EDGE,"E272"),sQuery(id+"F8.wireOp",EDGE,"E273"),sQuery(id+"F8.wireOp",EDGE,"E274"),sQuery(id+"F8.wireOp",EDGE,"E275"),sQuery(id+"F8.wireOp",EDGE,"E276"),sQuery(id+"F8.wireOp",EDGE,"E277"),sQuery(id+"F8.wireOp",EDGE,"E278"),sQuery(id+"F8.wireOp",EDGE,"E279"),sQuery(id+"F8.wireOp",EDGE,"E280"),sQuery(id+"F8.wireOp",EDGE,"E281"),sQuery(id+"F8.wireOp",EDGE,"E282"),sQuery(id+"F8.wireOp",EDGE,"E283"),sQuery(id+"F8.wireOp",EDGE,"E284"),sQuery(id+"F8.wireOp",EDGE,"E285"),sQuery(id+"F8.wireOp",EDGE,"E286"),sQuery(id+"F8.wireOp",EDGE,"E287"),sQuery(id+"F8.wireOp",EDGE,"E288"),sQuery(id+"F8.wireOp",EDGE,"E289"),sQuery(id+"F8.wireOp",EDGE,"E290"),sQuery(id+"F8.wireOp",EDGE,"E291"),sQuery(id+"F8.wireOp",EDGE,"E292"),sQuery(id+"F8.wireOp",EDGE,"E293"),sQuery(id+"F8.wireOp",EDGE,"E294"),sQuery(id+"F8.wireOp",EDGE,"E295")])]});
            var Q1;
            Q1=qCreatedBy(makeId("Origin.pointOp"),VERTEX);
            transform(context, id + "F10", {"entities" : qUnion([Q0]), "transformType" : TransformType.SCALE_UNIFORMLY, "scale" : .13, "scalePoint" : qUnion([Q1]), "makeCopy" : false});
        }
        {
            var Q0;
            Q0=makeQuery(id+"F9.opExtrude","SWEPT_BODY",BODY,{"disambiguationData":[OSD([sQuery(id+"F8.wireOp",EDGE,"E6"),sQuery(id+"F8.wireOp",EDGE,"E7"),sQuery(id+"F8.wireOp",EDGE,"E8"),sQuery(id+"F8.wireOp",EDGE,"E9"),sQuery(id+"F8.wireOp",EDGE,"E10"),sQuery(id+"F8.wireOp",EDGE,"E11"),sQuery(id+"F8.wireOp",EDGE,"E12"),sQuery(id+"F8.wireOp",EDGE,"E13"),sQuery(id+"F8.wireOp",EDGE,"E14"),sQuery(id+"F8.wireOp",EDGE,"E15"),sQuery(id+"F8.wireOp",EDGE,"E16"),sQuery(id+"F8.wireOp",EDGE,"E17"),sQuery(id+"F8.wireOp",EDGE,"E18"),sQuery(id+"F8.wireOp",EDGE,"E19"),sQuery(id+"F8.wireOp",EDGE,"E20"),sQuery(id+"F8.wireOp",EDGE,"E21"),sQuery(id+"F8.wireOp",EDGE,"E22"),sQuery(id+"F8.wireOp",EDGE,"E23"),sQuery(id+"F8.wireOp",EDGE,"E24"),sQuery(id+"F8.wireOp",EDGE,"E25"),sQuery(id+"F8.wireOp",EDGE,"E26"),sQuery(id+"F8.wireOp",EDGE,"E27"),sQuery(id+"F8.wireOp",EDGE,"E28"),sQuery(id+"F8.wireOp",EDGE,"E29"),sQuery(id+"F8.wireOp",EDGE,"E30"),sQuery(id+"F8.wireOp",EDGE,"E31"),sQuery(id+"F8.wireOp",EDGE,"E32"),sQuery(id+"F8.wireOp",EDGE,"E33"),sQuery(id+"F8.wireOp",EDGE,"E34"),sQuery(id+"F8.wireOp",EDGE,"E35"),sQuery(id+"F8.wireOp",EDGE,"E36"),sQuery(id+"F8.wireOp",EDGE,"E37"),sQuery(id+"F8.wireOp",EDGE,"E38"),sQuery(id+"F8.wireOp",EDGE,"E39"),sQuery(id+"F8.wireOp",EDGE,"E40"),sQuery(id+"F8.wireOp",EDGE,"E41"),sQuery(id+"F8.wireOp",EDGE,"E42"),sQuery(id+"F8.wireOp",EDGE,"E43"),sQuery(id+"F8.wireOp",EDGE,"E44"),sQuery(id+"F8.wireOp",EDGE,"E45"),sQuery(id+"F8.wireOp",EDGE,"E46"),sQuery(id+"F8.wireOp",EDGE,"E47"),sQuery(id+"F8.wireOp",EDGE,"E48"),sQuery(id+"F8.wireOp",EDGE,"E49"),sQuery(id+"F8.wireOp",EDGE,"E50"),sQuery(id+"F8.wireOp",EDGE,"E51"),sQuery(id+"F8.wireOp",EDGE,"E52"),sQuery(id+"F8.wireOp",EDGE,"E53"),sQuery(id+"F8.wireOp",EDGE,"E54"),sQuery(id+"F8.wireOp",EDGE,"E55"),sQuery(id+"F8.wireOp",EDGE,"E56"),sQuery(id+"F8.wireOp",EDGE,"E57"),sQuery(id+"F8.wireOp",EDGE,"E58"),sQuery(id+"F8.wireOp",EDGE,"E59"),sQuery(id+"F8.wireOp",EDGE,"E60"),sQuery(id+"F8.wireOp",EDGE,"E61"),sQuery(id+"F8.wireOp",EDGE,"E62"),sQuery(id+"F8.wireOp",EDGE,"E63"),sQuery(id+"F8.wireOp",EDGE,"E64"),sQuery(id+"F8.wireOp",EDGE,"E65"),sQuery(id+"F8.wireOp",EDGE,"E66"),sQuery(id+"F8.wireOp",EDGE,"E67"),sQuery(id+"F8.wireOp",EDGE,"E68"),sQuery(id+"F8.wireOp",EDGE,"E69"),sQuery(id+"F8.wireOp",EDGE,"E70"),sQuery(id+"F8.wireOp",EDGE,"E71"),sQuery(id+"F8.wireOp",EDGE,"E72"),sQuery(id+"F8.wireOp",EDGE,"E73"),sQuery(id+"F8.wireOp",EDGE,"E74"),sQuery(id+"F8.wireOp",EDGE,"E75"),sQuery(id+"F8.wireOp",EDGE,"E76"),sQuery(id+"F8.wireOp",EDGE,"E77"),sQuery(id+"F8.wireOp",EDGE,"E78"),sQuery(id+"F8.wireOp",EDGE,"E79"),sQuery(id+"F8.wireOp",EDGE,"E80"),sQuery(id+"F8.wireOp",EDGE,"E81"),sQuery(id+"F8.wireOp",EDGE,"E82"),sQuery(id+"F8.wireOp",EDGE,"E83"),sQuery(id+"F8.wireOp",EDGE,"E84"),sQuery(id+"F8.wireOp",EDGE,"E85"),sQuery(id+"F8.wireOp",EDGE,"E86"),sQuery(id+"F8.wireOp",EDGE,"E87"),sQuery(id+"F8.wireOp",EDGE,"E88"),sQuery(id+"F8.wireOp",EDGE,"E89"),sQuery(id+"F8.wireOp",EDGE,"E90"),sQuery(id+"F8.wireOp",EDGE,"E91"),sQuery(id+"F8.wireOp",EDGE,"E92"),sQuery(id+"F8.wireOp",EDGE,"E93"),sQuery(id+"F8.wireOp",EDGE,"E94"),sQuery(id+"F8.wireOp",EDGE,"E95"),sQuery(id+"F8.wireOp",EDGE,"E96"),sQuery(id+"F8.wireOp",EDGE,"E97"),sQuery(id+"F8.wireOp",EDGE,"E98"),sQuery(id+"F8.wireOp",EDGE,"E99"),sQuery(id+"F8.wireOp",EDGE,"E100"),sQuery(id+"F8.wireOp",EDGE,"E101"),sQuery(id+"F8.wireOp",EDGE,"E102"),sQuery(id+"F8.wireOp",EDGE,"E103"),sQuery(id+"F8.wireOp",EDGE,"E104"),sQuery(id+"F8.wireOp",EDGE,"E105"),sQuery(id+"F8.wireOp",EDGE,"E106"),sQuery(id+"F8.wireOp",EDGE,"E107"),sQuery(id+"F8.wireOp",EDGE,"E108"),sQuery(id+"F8.wireOp",EDGE,"E109"),sQuery(id+"F8.wireOp",EDGE,"E110"),sQuery(id+"F8.wireOp",EDGE,"E111"),sQuery(id+"F8.wireOp",EDGE,"E112"),sQuery(id+"F8.wireOp",EDGE,"E113"),sQuery(id+"F8.wireOp",EDGE,"E114"),sQuery(id+"F8.wireOp",EDGE,"E115"),sQuery(id+"F8.wireOp",EDGE,"E116"),sQuery(id+"F8.wireOp",EDGE,"E117"),sQuery(id+"F8.wireOp",EDGE,"E118"),sQuery(id+"F8.wireOp",EDGE,"E119"),sQuery(id+"F8.wireOp",EDGE,"E120"),sQuery(id+"F8.wireOp",EDGE,"E121"),sQuery(id+"F8.wireOp",EDGE,"E122"),sQuery(id+"F8.wireOp",EDGE,"E123"),sQuery(id+"F8.wireOp",EDGE,"E124"),sQuery(id+"F8.wireOp",EDGE,"E125"),sQuery(id+"F8.wireOp",EDGE,"E126"),sQuery(id+"F8.wireOp",EDGE,"E127"),sQuery(id+"F8.wireOp",EDGE,"E128"),sQuery(id+"F8.wireOp",EDGE,"E129"),sQuery(id+"F8.wireOp",EDGE,"E130"),sQuery(id+"F8.wireOp",EDGE,"E131"),sQuery(id+"F8.wireOp",EDGE,"E132"),sQuery(id+"F8.wireOp",EDGE,"E133"),sQuery(id+"F8.wireOp",EDGE,"E134"),sQuery(id+"F8.wireOp",EDGE,"E135"),sQuery(id+"F8.wireOp",EDGE,"E136"),sQuery(id+"F8.wireOp",EDGE,"E137"),sQuery(id+"F8.wireOp",EDGE,"E138"),sQuery(id+"F8.wireOp",EDGE,"E139"),sQuery(id+"F8.wireOp",EDGE,"E140"),sQuery(id+"F8.wireOp",EDGE,"E141"),sQuery(id+"F8.wireOp",EDGE,"E142"),sQuery(id+"F8.wireOp",EDGE,"E143"),sQuery(id+"F8.wireOp",EDGE,"E144"),sQuery(id+"F8.wireOp",EDGE,"E145"),sQuery(id+"F8.wireOp",EDGE,"E146"),sQuery(id+"F8.wireOp",EDGE,"E147"),sQuery(id+"F8.wireOp",EDGE,"E148"),sQuery(id+"F8.wireOp",EDGE,"E149"),sQuery(id+"F8.wireOp",EDGE,"E150"),sQuery(id+"F8.wireOp",EDGE,"E151"),sQuery(id+"F8.wireOp",EDGE,"E152"),sQuery(id+"F8.wireOp",EDGE,"E153"),sQuery(id+"F8.wireOp",EDGE,"E154"),sQuery(id+"F8.wireOp",EDGE,"E155"),sQuery(id+"F8.wireOp",EDGE,"E156"),sQuery(id+"F8.wireOp",EDGE,"E157"),sQuery(id+"F8.wireOp",EDGE,"E158"),sQuery(id+"F8.wireOp",EDGE,"E159"),sQuery(id+"F8.wireOp",EDGE,"E160"),sQuery(id+"F8.wireOp",EDGE,"E161"),sQuery(id+"F8.wireOp",EDGE,"E162"),sQuery(id+"F8.wireOp",EDGE,"E163"),sQuery(id+"F8.wireOp",EDGE,"E164"),sQuery(id+"F8.wireOp",EDGE,"E165"),sQuery(id+"F8.wireOp",EDGE,"E166"),sQuery(id+"F8.wireOp",EDGE,"E167"),sQuery(id+"F8.wireOp",EDGE,"E168"),sQuery(id+"F8.wireOp",EDGE,"E169"),sQuery(id+"F8.wireOp",EDGE,"E170"),sQuery(id+"F8.wireOp",EDGE,"E171"),sQuery(id+"F8.wireOp",EDGE,"E172"),sQuery(id+"F8.wireOp",EDGE,"E173"),sQuery(id+"F8.wireOp",EDGE,"E174"),sQuery(id+"F8.wireOp",EDGE,"E175"),sQuery(id+"F8.wireOp",EDGE,"E176"),sQuery(id+"F8.wireOp",EDGE,"E177"),sQuery(id+"F8.wireOp",EDGE,"E178"),sQuery(id+"F8.wireOp",EDGE,"E179"),sQuery(id+"F8.wireOp",EDGE,"E180"),sQuery(id+"F8.wireOp",EDGE,"E181"),sQuery(id+"F8.wireOp",EDGE,"E182"),sQuery(id+"F8.wireOp",EDGE,"E183"),sQuery(id+"F8.wireOp",EDGE,"E184"),sQuery(id+"F8.wireOp",EDGE,"E185"),sQuery(id+"F8.wireOp",EDGE,"E186"),sQuery(id+"F8.wireOp",EDGE,"E187"),sQuery(id+"F8.wireOp",EDGE,"E188"),sQuery(id+"F8.wireOp",EDGE,"E189"),sQuery(id+"F8.wireOp",EDGE,"E190"),sQuery(id+"F8.wireOp",EDGE,"E191"),sQuery(id+"F8.wireOp",EDGE,"E192"),sQuery(id+"F8.wireOp",EDGE,"E193"),sQuery(id+"F8.wireOp",EDGE,"E194"),sQuery(id+"F8.wireOp",EDGE,"E195"),sQuery(id+"F8.wireOp",EDGE,"E196"),sQuery(id+"F8.wireOp",EDGE,"E197"),sQuery(id+"F8.wireOp",EDGE,"E198"),sQuery(id+"F8.wireOp",EDGE,"E199"),sQuery(id+"F8.wireOp",EDGE,"E200"),sQuery(id+"F8.wireOp",EDGE,"E201"),sQuery(id+"F8.wireOp",EDGE,"E202"),sQuery(id+"F8.wireOp",EDGE,"E203"),sQuery(id+"F8.wireOp",EDGE,"E204"),sQuery(id+"F8.wireOp",EDGE,"E205"),sQuery(id+"F8.wireOp",EDGE,"E206"),sQuery(id+"F8.wireOp",EDGE,"E207"),sQuery(id+"F8.wireOp",EDGE,"E208"),sQuery(id+"F8.wireOp",EDGE,"E209"),sQuery(id+"F8.wireOp",EDGE,"E210"),sQuery(id+"F8.wireOp",EDGE,"E211"),sQuery(id+"F8.wireOp",EDGE,"E212"),sQuery(id+"F8.wireOp",EDGE,"E213"),sQuery(id+"F8.wireOp",EDGE,"E214"),sQuery(id+"F8.wireOp",EDGE,"E215"),sQuery(id+"F8.wireOp",EDGE,"E216"),sQuery(id+"F8.wireOp",EDGE,"E217"),sQuery(id+"F8.wireOp",EDGE,"E218"),sQuery(id+"F8.wireOp",EDGE,"E219"),sQuery(id+"F8.wireOp",EDGE,"E220"),sQuery(id+"F8.wireOp",EDGE,"E221"),sQuery(id+"F8.wireOp",EDGE,"E222"),sQuery(id+"F8.wireOp",EDGE,"E223"),sQuery(id+"F8.wireOp",EDGE,"E224"),sQuery(id+"F8.wireOp",EDGE,"E225"),sQuery(id+"F8.wireOp",EDGE,"E226"),sQuery(id+"F8.wireOp",EDGE,"E227"),sQuery(id+"F8.wireOp",EDGE,"E228"),sQuery(id+"F8.wireOp",EDGE,"E229"),sQuery(id+"F8.wireOp",EDGE,"E230"),sQuery(id+"F8.wireOp",EDGE,"E231"),sQuery(id+"F8.wireOp",EDGE,"E232"),sQuery(id+"F8.wireOp",EDGE,"E233"),sQuery(id+"F8.wireOp",EDGE,"E234"),sQuery(id+"F8.wireOp",EDGE,"E235"),sQuery(id+"F8.wireOp",EDGE,"E236"),sQuery(id+"F8.wireOp",EDGE,"E237"),sQuery(id+"F8.wireOp",EDGE,"E238"),sQuery(id+"F8.wireOp",EDGE,"E239"),sQuery(id+"F8.wireOp",EDGE,"E240"),sQuery(id+"F8.wireOp",EDGE,"E241"),sQuery(id+"F8.wireOp",EDGE,"E242"),sQuery(id+"F8.wireOp",EDGE,"E243"),sQuery(id+"F8.wireOp",EDGE,"E244"),sQuery(id+"F8.wireOp",EDGE,"E245"),sQuery(id+"F8.wireOp",EDGE,"E246"),sQuery(id+"F8.wireOp",EDGE,"E247"),sQuery(id+"F8.wireOp",EDGE,"E248"),sQuery(id+"F8.wireOp",EDGE,"E249"),sQuery(id+"F8.wireOp",EDGE,"E250"),sQuery(id+"F8.wireOp",EDGE,"E251"),sQuery(id+"F8.wireOp",EDGE,"E252"),sQuery(id+"F8.wireOp",EDGE,"E253"),sQuery(id+"F8.wireOp",EDGE,"E254"),sQuery(id+"F8.wireOp",EDGE,"E255"),sQuery(id+"F8.wireOp",EDGE,"E256"),sQuery(id+"F8.wireOp",EDGE,"E257"),sQuery(id+"F8.wireOp",EDGE,"E258"),sQuery(id+"F8.wireOp",EDGE,"E259"),sQuery(id+"F8.wireOp",EDGE,"E260"),sQuery(id+"F8.wireOp",EDGE,"E261"),sQuery(id+"F8.wireOp",EDGE,"E262"),sQuery(id+"F8.wireOp",EDGE,"E263"),sQuery(id+"F8.wireOp",EDGE,"E264"),sQuery(id+"F8.wireOp",EDGE,"E265"),sQuery(id+"F8.wireOp",EDGE,"E266"),sQuery(id+"F8.wireOp",EDGE,"E267"),sQuery(id+"F8.wireOp",EDGE,"E268"),sQuery(id+"F8.wireOp",EDGE,"E269"),sQuery(id+"F8.wireOp",EDGE,"E270"),sQuery(id+"F8.wireOp",EDGE,"E271"),sQuery(id+"F8.wireOp",EDGE,"E272"),sQuery(id+"F8.wireOp",EDGE,"E273"),sQuery(id+"F8.wireOp",EDGE,"E274"),sQuery(id+"F8.wireOp",EDGE,"E275"),sQuery(id+"F8.wireOp",EDGE,"E276"),sQuery(id+"F8.wireOp",EDGE,"E277"),sQuery(id+"F8.wireOp",EDGE,"E278"),sQuery(id+"F8.wireOp",EDGE,"E279"),sQuery(id+"F8.wireOp",EDGE,"E280"),sQuery(id+"F8.wireOp",EDGE,"E281"),sQuery(id+"F8.wireOp",EDGE,"E282"),sQuery(id+"F8.wireOp",EDGE,"E283"),sQuery(id+"F8.wireOp",EDGE,"E284"),sQuery(id+"F8.wireOp",EDGE,"E285"),sQuery(id+"F8.wireOp",EDGE,"E286"),sQuery(id+"F8.wireOp",EDGE,"E287"),sQuery(id+"F8.wireOp",EDGE,"E288"),sQuery(id+"F8.wireOp",EDGE,"E289"),sQuery(id+"F8.wireOp",EDGE,"E290"),sQuery(id+"F8.wireOp",EDGE,"E291"),sQuery(id+"F8.wireOp",EDGE,"E292"),sQuery(id+"F8.wireOp",EDGE,"E293"),sQuery(id+"F8.wireOp",EDGE,"E294"),sQuery(id+"F8.wireOp",EDGE,"E295")])]});
            transform(context, id + "F11", {"entities" : qUnion([Q0]), "transformType" : TransformType.TRANSLATION_3D, "dx" : 0 * mm, "dy" : 0 * mm, "dz" : 4 * mm, "makeCopy" : false});
        }
        {
            var Q0;
            Q0=makeQuery(id+"F6.opRevolve","SWEPT_BODY",BODY,{"disambiguationData":[OSD([sQuery(id+"F5.wireOp",EDGE,"E3"),sQuery(id+"F5.wireOp",EDGE,"E4"),sQuery(id+"F5.wireOp",EDGE,"E5")])]});
            transform(context, id + "F12", {"entities" : qUnion([Q0]), "transformType" : TransformType.TRANSLATION_3D, "dx" : 0 * mm, "dy" : 0 * mm, "dz" : 0 * mm, "makeCopy" : true});
        }
        {
            var Q0;
            Q0=makeQuery(id+"F12.opPattern","COPY",BODY,{"derivedFrom":makeQuery(id+"F6.opRevolve","SWEPT_BODY",BODY,{"disambiguationData":[OSD([sQuery(id+"F5.wireOp",EDGE,"E3"),sQuery(id+"F5.wireOp",EDGE,"E4"),sQuery(id+"F5.wireOp",EDGE,"E5")])]}),"instanceName":"1"});
            transform(context, id + "F13", {"entities" : qUnion([Q0]), "transformType" : TransformType.TRANSLATION_3D, "dx" : 0 * mm, "dy" : 0 * mm, "dz" : 0 * mm, "makeCopy" : true});
        }
        {
            var Q0;
            Q0=makeQuery(id+"F13.opPattern","COPY",BODY,{"derivedFrom":makeQuery(id+"F12.opPattern","COPY",BODY,{"derivedFrom":makeQuery(id+"F6.opRevolve","SWEPT_BODY",BODY,{"disambiguationData":[OSD([sQuery(id+"F5.wireOp",EDGE,"E3"),sQuery(id+"F5.wireOp",EDGE,"E4"),sQuery(id+"F5.wireOp",EDGE,"E5")])]}),"instanceName":"1"}),"instanceName":"1"});
            transform(context, id + "F14", {"entities" : qUnion([Q0]), "transformType" : TransformType.TRANSLATION_3D, "dx" : 0 * mm, "dy" : 0 * mm, "dz" : -4 * mm, "makeCopy" : false});
        }
        {
            var Q0;
            Q0=qCreatedBy(makeId("Top.planeOp"),FACE);
            var sketch = newSketch(context, id + "F15", { "sketchPlane" : qUnion([Q0])});
            skCircle(sketch, "E296", {"center": v(0, 0) * mm, "radius": 33 * mm});
            skSolve(sketch);
        }
        {
            var Q0;
            Q0 = qSketchRegion(id + "F15", true);
            extrude(context, id + "F16", {"entities" : qUnion([Q0]), "depth" : 3 * mm});
        }
        {
            var Q0;
            Q0=makeQuery(id+"F13.opPattern","COPY",BODY,{"derivedFrom":makeQuery(id+"F12.opPattern","COPY",BODY,{"derivedFrom":makeQuery(id+"F6.opRevolve","SWEPT_BODY",BODY,{"disambiguationData":[OSD([sQuery(id+"F5.wireOp",EDGE,"E3"),sQuery(id+"F5.wireOp",EDGE,"E4"),sQuery(id+"F5.wireOp",EDGE,"E5")])]}),"instanceName":"1"}),"instanceName":"1"});
            var Q1;
            Q1=makeQuery(id+"F16.opExtrude","SWEPT_BODY",BODY,{"disambiguationData":[OSD([sQuery(id+"F15.wireOp",EDGE,"E296")])]});
            booleanBodies(context, id + "F17", {"operationType" : BooleanOperationType.INTERSECTION, "tools" : qUnion([Q0, Q1])});
        }
        {
            var Q0;
            Q0=qCreatedBy(makeId("Top.planeOp"),FACE);
            var sketch = newSketch(context, id + "F18", { "sketchPlane" : qUnion([Q0])});
            skArc(sketch, "E297", {"start": v(-10.28, 35.23) * mm, "mid": v(-12.4, 34.37) * mm, "end": v(-14.44, 33.36) * mm});
            skArc(sketch, "E298", {"start": v(-14.44, 33.36) * mm, "mid": v(-16.42, 32.18) * mm, "end": v(-18.3, 30.85) * mm});
            skArc(sketch, "E299", {"start": v(-18.3, 30.85) * mm, "mid": v(-19.99, 29.43) * mm, "end": v(-21.56, 27.88) * mm});
            skArc(sketch, "E300", {"start": v(-21.56, 27.88) * mm, "mid": v(-22.88, 26.33) * mm, "end": v(-24.02, 24.65) * mm});
            skArc(sketch, "E301", {"start": v(-24.02, 24.65) * mm, "mid": v(-24.53, 23.82) * mm, "end": v(-25.04, 23) * mm});
            skArc(sketch, "E302", {"start": v(-25.04, 23) * mm, "mid": v(-25.55, 22.17) * mm, "end": v(-26.06, 21.35) * mm});
            skArc(sketch, "E303", {"start": v(-26.06, 21.35) * mm, "mid": v(-26.5, 20.63) * mm, "end": v(-26.96, 19.92) * mm});
            skArc(sketch, "E304", {"start": v(-26.96, 19.92) * mm, "mid": v(-27.23, 19.5) * mm, "end": v(-27.51, 19.08) * mm});
            skArc(sketch, "E305", {"start": v(-27.51, 19.08) * mm, "mid": v(-28.3, 18.24) * mm, "end": v(-29.34, 17.72) * mm});
            skArc(sketch, "E306", {"start": v(-29.34, 17.72) * mm, "mid": v(-31.11, 17.26) * mm, "end": v(-32.92, 16.97) * mm});
            skArc(sketch, "E307", {"start": v(-32.92, 16.97) * mm, "mid": v(-34.83, 16.84) * mm, "end": v(-36.75, 16.9) * mm});
            skArc(sketch, "E308", {"start": v(-36.75, 16.9) * mm, "mid": v(-38.18, 17.15) * mm, "end": v(-39.53, 17.7) * mm});
            skArc(sketch, "E309", {"start": v(-39.53, 17.7) * mm, "mid": v(-40.46, 18.27) * mm, "end": v(-41.31, 18.94) * mm});
            skArc(sketch, "E310", {"start": v(-41.31, 18.94) * mm, "mid": v(-41.72, 19.5) * mm, "end": v(-41.86, 20.17) * mm});
            skArc(sketch, "E311", {"start": v(-41.86, 20.17) * mm, "mid": v(-41.72, 20.83) * mm, "end": v(-41.3, 21.36) * mm});
            skArc(sketch, "E312", {"start": v(-41.3, 21.36) * mm, "mid": v(-40.46, 21.97) * mm, "end": v(-39.54, 22.46) * mm});
            skArc(sketch, "E313", {"start": v(-39.54, 22.46) * mm, "mid": v(-38.66, 22.95) * mm, "end": v(-37.87, 23.57) * mm});
            skArc(sketch, "E314", {"start": v(-37.87, 23.57) * mm, "mid": v(-36.97, 24.47) * mm, "end": v(-36.16, 25.44) * mm});
            skArc(sketch, "E315", {"start": v(-36.16, 25.44) * mm, "mid": v(-35.6, 26.24) * mm, "end": v(-35.13, 27.1) * mm});
            skArc(sketch, "E316", {"start": v(-35.13, 27.1) * mm, "mid": v(-35.16, 27.49) * mm, "end": v(-35.5, 27.67) * mm});
            skArc(sketch, "E317", {"start": v(-35.5, 27.67) * mm, "mid": v(-36.16, 27.59) * mm, "end": v(-36.8, 27.36) * mm});
            skArc(sketch, "E318", {"start": v(-36.8, 27.36) * mm, "mid": v(-38.02, 26.7) * mm, "end": v(-39.23, 26) * mm});
            skArc(sketch, "E319", {"start": v(-39.23, 26) * mm, "mid": v(-40.44, 25.24) * mm, "end": v(-41.6, 24.44) * mm});
            skArc(sketch, "E320", {"start": v(-41.6, 24.44) * mm, "mid": v(-42.33, 23.85) * mm, "end": v(-42.97, 23.18) * mm});
            skArc(sketch, "E321", {"start": v(-42.97, 23.18) * mm, "mid": v(-43.32, 22.8) * mm, "end": v(-43.7, 22.45) * mm});
            skArc(sketch, "E322", {"start": v(-43.7, 22.45) * mm, "mid": v(-44.25, 22.01) * mm, "end": v(-44.83, 21.6) * mm});
            skArc(sketch, "E323", {"start": v(-44.83, 21.6) * mm, "mid": v(-45.46, 21.17) * mm, "end": v(-46.12, 20.76) * mm});
            skArc(sketch, "E324", {"start": v(-46.12, 20.76) * mm, "mid": v(-46.75, 20.4) * mm, "end": v(-47.4, 20.07) * mm});
            skArc(sketch, "E325", {"start": v(-47.4, 20.07) * mm, "mid": v(-52.1, 17.75) * mm, "end": v(-56.73, 15.31) * mm});
            skArc(sketch, "E326", {"start": v(-56.73, 15.31) * mm, "mid": v(-58.07, 14.21) * mm, "end": v(-58.9, 12.7) * mm});
            skArc(sketch, "E327", {"start": v(-58.9, 12.7) * mm, "mid": v(-58.75, 11.51) * mm, "end": v(-57.76, 10.85) * mm});
            skArc(sketch, "E328", {"start": v(-57.76, 10.85) * mm, "mid": v(-54.16, 10.38) * mm, "end": v(-50.54, 10.12) * mm});
            skArc(sketch, "E329", {"start": v(-50.54, 10.12) * mm, "mid": v(-48.58, 10) * mm, "end": v(-46.62, 9.8) * mm});
            skArc(sketch, "E330", {"start": v(-46.62, 9.8) * mm, "mid": v(-45.38, 9.6) * mm, "end": v(-44.18, 9.22) * mm});
            skArc(sketch, "E331", {"start": v(-44.18, 9.22) * mm, "mid": v(-43.03, 8.7) * mm, "end": v(-41.95, 8.05) * mm});
            skArc(sketch, "E332", {"start": v(-41.95, 8.05) * mm, "mid": v(-40.34, 6.9) * mm, "end": v(-38.76, 5.7) * mm});
            skArc(sketch, "E333", {"start": v(-38.76, 5.7) * mm, "mid": v(-37.63, 4.83) * mm, "end": v(-36.45, 4.02) * mm});
            skArc(sketch, "E334", {"start": v(-36.45, 4.02) * mm, "mid": v(-35.13, 3.2) * mm, "end": v(-33.78, 2.42) * mm});
            skArc(sketch, "E335", {"start": v(-33.78, 2.42) * mm, "mid": v(-32.5, 1.74) * mm, "end": v(-31.18, 1.1) * mm});
            skArc(sketch, "E336", {"start": v(-31.18, 1.1) * mm, "mid": v(-30.15, 0.7) * mm, "end": v(-29.1, 0.36) * mm});
            skArc(sketch, "E337", {"start": v(-29.1, 0.36) * mm, "mid": v(-27.88, -0.01) * mm, "end": v(-26.69, -0.47) * mm});
            skArc(sketch, "E338", {"start": v(-26.69, -0.47) * mm, "mid": v(-25.73, -0.95) * mm, "end": v(-24.83, -1.55) * mm});
            skArc(sketch, "E339", {"start": v(-24.83, -1.55) * mm, "mid": v(-23.94, -2.3) * mm, "end": v(-23.14, -3.13) * mm});
            skArc(sketch, "E340", {"start": v(-23.14, -3.13) * mm, "mid": v(-22.14, -4.33) * mm, "end": v(-21.2, -5.58) * mm});
            skArc(sketch, "E341", {"start": v(-21.2, -5.58) * mm, "mid": v(-20.09, -7.06) * mm, "end": v(-18.9, -8.47) * mm});
            skArc(sketch, "E342", {"start": v(-18.9, -8.47) * mm, "mid": v(-18.05, -9.3) * mm, "end": v(-17.07, -9.96) * mm});
            skArc(sketch, "E343", {"start": v(-17.07, -9.96) * mm, "mid": v(-16.37, -10.2) * mm, "end": v(-15.63, -10.16) * mm});
            skArc(sketch, "E344", {"start": v(-15.63, -10.16) * mm, "mid": v(-14.97, -9.86) * mm, "end": v(-14.48, -9.33) * mm});
            skArc(sketch, "E345", {"start": v(-14.48, -9.33) * mm, "mid": v(-14.4, -9.15) * mm, "end": v(-14.4, -8.95) * mm});
            skArc(sketch, "E346", {"start": v(-14.4, -8.95) * mm, "mid": v(-14.46, -8.77) * mm, "end": v(-14.58, -8.62) * mm});
            skArc(sketch, "E347", {"start": v(-14.58, -8.62) * mm, "mid": v(-14.8, -8.49) * mm, "end": v(-15.04, -8.4) * mm});
            skArc(sketch, "E348", {"start": v(-15.04, -8.4) * mm, "mid": v(-15.38, -8.35) * mm, "end": v(-15.71, -8.33) * mm});
            skArc(sketch, "E349", {"start": v(-15.71, -8.33) * mm, "mid": v(-16.2, -8.26) * mm, "end": v(-16.64, -8.06) * mm});
            skArc(sketch, "E350", {"start": v(-16.64, -8.06) * mm, "mid": v(-17.07, -7.72) * mm, "end": v(-17.42, -7.3) * mm});
            skArc(sketch, "E351", {"start": v(-17.42, -7.3) * mm, "mid": v(-17.8, -6.65) * mm, "end": v(-18.1, -5.96) * mm});
            skArc(sketch, "E352", {"start": v(-18.1, -5.96) * mm, "mid": v(-18.46, -4.9) * mm, "end": v(-18.77, -3.82) * mm});
            skArc(sketch, "E353", {"start": v(-18.77, -3.82) * mm, "mid": v(-19.35, -1.53) * mm, "end": v(-19.89, 0.78) * mm});
            skArc(sketch, "E354", {"start": v(-19.89, 0.78) * mm, "mid": v(-19.96, 1.67) * mm, "end": v(-19.79, 2.55) * mm});
            skArc(sketch, "E355", {"start": v(-19.79, 2.55) * mm, "mid": v(-19.4, 3.12) * mm, "end": v(-18.78, 3.42) * mm});
            skArc(sketch, "E356", {"start": v(-18.78, 3.42) * mm, "mid": v(-17.48, 3.6) * mm, "end": v(-16.18, 3.67) * mm});
            skArc(sketch, "E357", {"start": v(-16.18, 3.67) * mm, "mid": v(-14.56, 3.58) * mm, "end": v(-12.96, 3.3) * mm});
            skArc(sketch, "E358", {"start": v(-12.96, 3.3) * mm, "mid": v(-11.95, 2.87) * mm, "end": v(-11.15, 2.13) * mm});
            skArc(sketch, "E359", {"start": v(-11.15, 2.13) * mm, "mid": v(-10.53, 1.04) * mm, "end": v(-10.23, -0.17) * mm});
            skArc(sketch, "E360", {"start": v(-10.23, -0.17) * mm, "mid": v(-10.04, -2.32) * mm, "end": v(-9.98, -4.48) * mm});
            skArc(sketch, "E361", {"start": v(-9.98, -4.48) * mm, "mid": v(-10.16, -9.11) * mm, "end": v(-10.7, -13.72) * mm});
            skArc(sketch, "E362", {"start": v(-10.7, -13.72) * mm, "mid": v(-11.56, -17.1) * mm, "end": v(-13, -20.26) * mm});
            skArc(sketch, "E363", {"start": v(-13, -20.26) * mm, "mid": v(-14.9, -22.9) * mm, "end": v(-17.28, -25.1) * mm});
            skArc(sketch, "E364", {"start": v(-17.28, -25.1) * mm, "mid": v(-20.54, -27.25) * mm, "end": v(-24.04, -29.02) * mm});
            skArc(sketch, "E365", {"start": v(-24.04, -29.02) * mm, "mid": v(-25.28, -29.59) * mm, "end": v(-26.5, -30.21) * mm});
            skArc(sketch, "E366", {"start": v(-26.5, -30.21) * mm, "mid": v(-27.53, -30.8) * mm, "end": v(-28.51, -31.47) * mm});
            skArc(sketch, "E367", {"start": v(-28.51, -31.47) * mm, "mid": v(-29.28, -32.07) * mm, "end": v(-30, -32.73) * mm});
            skArc(sketch, "E368", {"start": v(-30, -32.73) * mm, "mid": v(-30.47, -33.28) * mm, "end": v(-30.83, -33.9) * mm});
            skArc(sketch, "E369", {"start": v(-30.83, -33.9) * mm, "mid": v(-31.04, -34.79) * mm, "end": v(-30.9, -35.68) * mm});
            skArc(sketch, "E370", {"start": v(-30.9, -35.68) * mm, "mid": v(-30.43, -36.22) * mm, "end": v(-29.72, -36.33) * mm});
            skArc(sketch, "E371", {"start": v(-29.72, -36.33) * mm, "mid": v(-28.22, -35.88) * mm, "end": v(-26.83, -35.15) * mm});
            skArc(sketch, "E372", {"start": v(-26.83, -35.15) * mm, "mid": v(-24.76, -33.75) * mm, "end": v(-22.76, -32.25) * mm});
            skArc(sketch, "E373", {"start": v(-22.76, -32.25) * mm, "mid": v(-21.6, -31.36) * mm, "end": v(-20.41, -30.5) * mm});
            skArc(sketch, "E374", {"start": v(-20.41, -30.5) * mm, "mid": v(-19.03, -29.55) * mm, "end": v(-17.62, -28.62) * mm});
            skArc(sketch, "E375", {"start": v(-17.62, -28.62) * mm, "mid": v(-16.24, -27.74) * mm, "end": v(-14.84, -26.89) * mm});
            skArc(sketch, "E376", {"start": v(-14.84, -26.89) * mm, "mid": v(-13.7, -26.23) * mm, "end": v(-12.54, -25.62) * mm});
            skArc(sketch, "E377", {"start": v(-12.54, -25.62) * mm, "mid": v(-11.53, -25.1) * mm, "end": v(-10.54, -24.56) * mm});
            skArc(sketch, "E378", {"start": v(-10.54, -24.56) * mm, "mid": v(-9.64, -24.04) * mm, "end": v(-8.75, -23.49) * mm});
            skArc(sketch, "E379", {"start": v(-8.75, -23.49) * mm, "mid": v(-8.02, -23.01) * mm, "end": v(-7.3, -22.52) * mm});
            skArc(sketch, "E380", {"start": v(-7.3, -22.52) * mm, "mid": v(-7, -22.26) * mm, "end": v(-6.74, -21.95) * mm});
            skArc(sketch, "E381", {"start": v(-6.74, -21.95) * mm, "mid": v(-6.55, -21.57) * mm, "end": v(-6.45, -21.16) * mm});
            skArc(sketch, "E382", {"start": v(-6.45, -21.16) * mm, "mid": v(-6.32, -20.06) * mm, "end": v(-6.2, -18.96) * mm});
            skArc(sketch, "E383", {"start": v(-6.2, -18.96) * mm, "mid": v(-6.1, -17.62) * mm, "end": v(-6.02, -16.28) * mm});
            skArc(sketch, "E384", {"start": v(-6.02, -16.28) * mm, "mid": v(-5.96, -14.8) * mm, "end": v(-5.94, -13.33) * mm});
            skArc(sketch, "E385", {"start": v(-5.94, -13.33) * mm, "mid": v(-5.83, -9.86) * mm, "end": v(-5.57, -6.4) * mm});
            skArc(sketch, "E386", {"start": v(-5.57, -6.4) * mm, "mid": v(-5.18, -4.17) * mm, "end": v(-4.47, -2.02) * mm});
            skArc(sketch, "E387", {"start": v(-4.47, -2.02) * mm, "mid": v(-3.6, -0.37) * mm, "end": v(-2.4, 1.06) * mm});
            skArc(sketch, "E388", {"start": v(-2.4, 1.06) * mm, "mid": v(-0.77, 2.43) * mm, "end": v(1.02, 3.57) * mm});
            skArc(sketch, "E389", {"start": v(1.02, 3.57) * mm, "mid": v(2.07, 4.16) * mm, "end": v(3.1, 4.78) * mm});
            skArc(sketch, "E390", {"start": v(3.1, 4.78) * mm, "mid": v(4.37, 5.59) * mm, "end": v(5.64, 6.42) * mm});
            skArc(sketch, "E391", {"start": v(5.64, 6.42) * mm, "mid": v(6.93, 7.3) * mm, "end": v(8.2, 8.2) * mm});
            skArc(sketch, "E392", {"start": v(8.2, 8.2) * mm, "mid": v(9.32, 9) * mm, "end": v(10.4, 9.84) * mm});
            skArc(sketch, "E393", {"start": v(10.4, 9.84) * mm, "mid": v(11.4, 10.59) * mm, "end": v(12.4, 11.3) * mm});
            skArc(sketch, "E394", {"start": v(12.4, 11.3) * mm, "mid": v(13.39, 11.94) * mm, "end": v(14.4, 12.54) * mm});
            skArc(sketch, "E395", {"start": v(14.4, 12.54) * mm, "mid": v(15.25, 13.01) * mm, "end": v(16.12, 13.45) * mm});
            skArc(sketch, "E396", {"start": v(16.12, 13.45) * mm, "mid": v(16.6, 13.61) * mm, "end": v(17.12, 13.67) * mm});
            skArc(sketch, "E397", {"start": v(17.12, 13.67) * mm, "mid": v(17.63, 13.62) * mm, "end": v(18.12, 13.49) * mm});
            skArc(sketch, "E398", {"start": v(18.12, 13.49) * mm, "mid": v(18.97, 13.15) * mm, "end": v(19.8, 12.79) * mm});
            skArc(sketch, "E399", {"start": v(19.8, 12.79) * mm, "mid": v(20.78, 12.32) * mm, "end": v(21.74, 11.82) * mm});
            skArc(sketch, "E400", {"start": v(21.74, 11.82) * mm, "mid": v(22.73, 11.26) * mm, "end": v(23.69, 10.67) * mm});
            skArc(sketch, "E401", {"start": v(23.69, 10.67) * mm, "mid": v(25.86, 9.37) * mm, "end": v(28.1, 8.19) * mm});
            skArc(sketch, "E402", {"start": v(28.1, 8.19) * mm, "mid": v(30.55, 7.04) * mm, "end": v(33.05, 6) * mm});
            skArc(sketch, "E403", {"start": v(33.05, 6) * mm, "mid": v(35.54, 5.08) * mm, "end": v(38.07, 4.28) * mm});
            skArc(sketch, "E404", {"start": v(38.07, 4.28) * mm, "mid": v(40.37, 3.67) * mm, "end": v(42.7, 3.21) * mm});
            skArc(sketch, "E405", {"start": v(42.7, 3.21) * mm, "mid": v(44.96, 3.02) * mm, "end": v(47.21, 3.17) * mm});
            skArc(sketch, "E406", {"start": v(47.21, 3.17) * mm, "mid": v(49.49, 3.68) * mm, "end": v(51.66, 4.5) * mm});
            skArc(sketch, "E407", {"start": v(51.66, 4.5) * mm, "mid": v(53.59, 5.58) * mm, "end": v(55.32, 6.93) * mm});
            skArc(sketch, "E408", {"start": v(55.32, 6.93) * mm, "mid": v(56.61, 8.4) * mm, "end": v(57.56, 10.1) * mm});
            skArc(sketch, "E409", {"start": v(57.56, 10.1) * mm, "mid": v(58.12, 11.56) * mm, "end": v(58.6, 13.06) * mm});
            skArc(sketch, "E410", {"start": v(58.6, 13.06) * mm, "mid": v(58.86, 14.23) * mm, "end": v(58.96, 15.43) * mm});
            skArc(sketch, "E411", {"start": v(58.96, 15.43) * mm, "mid": v(58.8, 15.69) * mm, "end": v(58.5, 15.64) * mm});
            skArc(sketch, "E412", {"start": v(58.5, 15.64) * mm, "mid": v(58.03, 15.12) * mm, "end": v(57.68, 14.51) * mm});
            skArc(sketch, "E413", {"start": v(57.68, 14.51) * mm, "mid": v(56.8, 12.75) * mm, "end": v(55.79, 11.06) * mm});
            skArc(sketch, "E414", {"start": v(55.79, 11.06) * mm, "mid": v(54.87, 9.94) * mm, "end": v(53.74, 9.04) * mm});
            skArc(sketch, "E415", {"start": v(53.74, 9.04) * mm, "mid": v(52.45, 8.38) * mm, "end": v(51.05, 8) * mm});
            skArc(sketch, "E416", {"start": v(51.05, 8) * mm, "mid": v(49.08, 7.75) * mm, "end": v(47.1, 7.67) * mm});
            skArc(sketch, "E417", {"start": v(47.1, 7.67) * mm, "mid": v(44.31, 7.88) * mm, "end": v(41.6, 8.51) * mm});
            skArc(sketch, "E418", {"start": v(41.6, 8.51) * mm, "mid": v(38.64, 9.61) * mm, "end": v(35.83, 11.02) * mm});
            skArc(sketch, "E419", {"start": v(35.83, 11.02) * mm, "mid": v(32.28, 13.2) * mm, "end": v(28.9, 15.65) * mm});
            skArc(sketch, "E420", {"start": v(28.9, 15.65) * mm, "mid": v(24.14, 19.44) * mm, "end": v(19.47, 23.35) * mm});
            skArc(sketch, "E421", {"start": v(19.47, 23.35) * mm, "mid": v(14.64, 27.35) * mm, "end": v(9.65, 31.17) * mm});
            skArc(sketch, "E422", {"start": v(9.65, 31.17) * mm, "mid": v(6.18, 33.39) * mm, "end": v(2.47, 35.15) * mm});
            skArc(sketch, "E423", {"start": v(2.47, 35.15) * mm, "mid": v(-0.6, 36.05) * mm, "end": v(-3.78, 36.35) * mm});
            skArc(sketch, "E424", {"start": v(-3.78, 36.35) * mm, "mid": v(-7.08, 36.07) * mm, "end": v(-10.28, 35.23) * mm});
            skSolve(sketch);
        }
        {
            var Q0;
            Q0 = qSketchRegion(id + "F18", true);
            extrude(context, id + "F19", {"entities" : qUnion([Q0]), "depth" : 50 * mm});
        }
        {
            var Q0;
            Q0=makeQuery(id+"F19.opExtrude","SWEPT_BODY",BODY,{"disambiguationData":[OSD([sQuery(id+"F18.wireOp",EDGE,"E297"),sQuery(id+"F18.wireOp",EDGE,"E298"),sQuery(id+"F18.wireOp",EDGE,"E299"),sQuery(id+"F18.wireOp",EDGE,"E300"),sQuery(id+"F18.wireOp",EDGE,"E301"),sQuery(id+"F18.wireOp",EDGE,"E302"),sQuery(id+"F18.wireOp",EDGE,"E303"),sQuery(id+"F18.wireOp",EDGE,"E304"),sQuery(id+"F18.wireOp",EDGE,"E305"),sQuery(id+"F18.wireOp",EDGE,"E306"),sQuery(id+"F18.wireOp",EDGE,"E307"),sQuery(id+"F18.wireOp",EDGE,"E308"),sQuery(id+"F18.wireOp",EDGE,"E309"),sQuery(id+"F18.wireOp",EDGE,"E310"),sQuery(id+"F18.wireOp",EDGE,"E311"),sQuery(id+"F18.wireOp",EDGE,"E312"),sQuery(id+"F18.wireOp",EDGE,"E313"),sQuery(id+"F18.wireOp",EDGE,"E314"),sQuery(id+"F18.wireOp",EDGE,"E315"),sQuery(id+"F18.wireOp",EDGE,"E316"),sQuery(id+"F18.wireOp",EDGE,"E317"),sQuery(id+"F18.wireOp",EDGE,"E318"),sQuery(id+"F18.wireOp",EDGE,"E319"),sQuery(id+"F18.wireOp",EDGE,"E320"),sQuery(id+"F18.wireOp",EDGE,"E321"),sQuery(id+"F18.wireOp",EDGE,"E322"),sQuery(id+"F18.wireOp",EDGE,"E323"),sQuery(id+"F18.wireOp",EDGE,"E324"),sQuery(id+"F18.wireOp",EDGE,"E325"),sQuery(id+"F18.wireOp",EDGE,"E326"),sQuery(id+"F18.wireOp",EDGE,"E327"),sQuery(id+"F18.wireOp",EDGE,"E328"),sQuery(id+"F18.wireOp",EDGE,"E329"),sQuery(id+"F18.wireOp",EDGE,"E330"),sQuery(id+"F18.wireOp",EDGE,"E331"),sQuery(id+"F18.wireOp",EDGE,"E332"),sQuery(id+"F18.wireOp",EDGE,"E333"),sQuery(id+"F18.wireOp",EDGE,"E334"),sQuery(id+"F18.wireOp",EDGE,"E335"),sQuery(id+"F18.wireOp",EDGE,"E336"),sQuery(id+"F18.wireOp",EDGE,"E337"),sQuery(id+"F18.wireOp",EDGE,"E338"),sQuery(id+"F18.wireOp",EDGE,"E339"),sQuery(id+"F18.wireOp",EDGE,"E340"),sQuery(id+"F18.wireOp",EDGE,"E341"),sQuery(id+"F18.wireOp",EDGE,"E342"),sQuery(id+"F18.wireOp",EDGE,"E343"),sQuery(id+"F18.wireOp",EDGE,"E344"),sQuery(id+"F18.wireOp",EDGE,"E345"),sQuery(id+"F18.wireOp",EDGE,"E346"),sQuery(id+"F18.wireOp",EDGE,"E347"),sQuery(id+"F18.wireOp",EDGE,"E348"),sQuery(id+"F18.wireOp",EDGE,"E349"),sQuery(id+"F18.wireOp",EDGE,"E350"),sQuery(id+"F18.wireOp",EDGE,"E351"),sQuery(id+"F18.wireOp",EDGE,"E352"),sQuery(id+"F18.wireOp",EDGE,"E353"),sQuery(id+"F18.wireOp",EDGE,"E354"),sQuery(id+"F18.wireOp",EDGE,"E355"),sQuery(id+"F18.wireOp",EDGE,"E356"),sQuery(id+"F18.wireOp",EDGE,"E357"),sQuery(id+"F18.wireOp",EDGE,"E358"),sQuery(id+"F18.wireOp",EDGE,"E359"),sQuery(id+"F18.wireOp",EDGE,"E360"),sQuery(id+"F18.wireOp",EDGE,"E361"),sQuery(id+"F18.wireOp",EDGE,"E362"),sQuery(id+"F18.wireOp",EDGE,"E363"),sQuery(id+"F18.wireOp",EDGE,"E364"),sQuery(id+"F18.wireOp",EDGE,"E365"),sQuery(id+"F18.wireOp",EDGE,"E366"),sQuery(id+"F18.wireOp",EDGE,"E367"),sQuery(id+"F18.wireOp",EDGE,"E368"),sQuery(id+"F18.wireOp",EDGE,"E369"),sQuery(id+"F18.wireOp",EDGE,"E370"),sQuery(id+"F18.wireOp",EDGE,"E371"),sQuery(id+"F18.wireOp",EDGE,"E372"),sQuery(id+"F18.wireOp",EDGE,"E373"),sQuery(id+"F18.wireOp",EDGE,"E374"),sQuery(id+"F18.wireOp",EDGE,"E375"),sQuery(id+"F18.wireOp",EDGE,"E376"),sQuery(id+"F18.wireOp",EDGE,"E377"),sQuery(id+"F18.wireOp",EDGE,"E378"),sQuery(id+"F18.wireOp",EDGE,"E379"),sQuery(id+"F18.wireOp",EDGE,"E380"),sQuery(id+"F18.wireOp",EDGE,"E381"),sQuery(id+"F18.wireOp",EDGE,"E382"),sQuery(id+"F18.wireOp",EDGE,"E383"),sQuery(id+"F18.wireOp",EDGE,"E384"),sQuery(id+"F18.wireOp",EDGE,"E385"),sQuery(id+"F18.wireOp",EDGE,"E386"),sQuery(id+"F18.wireOp",EDGE,"E387"),sQuery(id+"F18.wireOp",EDGE,"E388"),sQuery(id+"F18.wireOp",EDGE,"E389"),sQuery(id+"F18.wireOp",EDGE,"E390"),sQuery(id+"F18.wireOp",EDGE,"E391"),sQuery(id+"F18.wireOp",EDGE,"E392"),sQuery(id+"F18.wireOp",EDGE,"E393"),sQuery(id+"F18.wireOp",EDGE,"E394"),sQuery(id+"F18.wireOp",EDGE,"E395"),sQuery(id+"F18.wireOp",EDGE,"E396"),sQuery(id+"F18.wireOp",EDGE,"E397"),sQuery(id+"F18.wireOp",EDGE,"E398"),sQuery(id+"F18.wireOp",EDGE,"E399"),sQuery(id+"F18.wireOp",EDGE,"E400"),sQuery(id+"F18.wireOp",EDGE,"E401"),sQuery(id+"F18.wireOp",EDGE,"E402"),sQuery(id+"F18.wireOp",EDGE,"E403"),sQuery(id+"F18.wireOp",EDGE,"E404"),sQuery(id+"F18.wireOp",EDGE,"E405"),sQuery(id+"F18.wireOp",EDGE,"E406"),sQuery(id+"F18.wireOp",EDGE,"E407"),sQuery(id+"F18.wireOp",EDGE,"E408"),sQuery(id+"F18.wireOp",EDGE,"E409"),sQuery(id+"F18.wireOp",EDGE,"E410"),sQuery(id+"F18.wireOp",EDGE,"E411"),sQuery(id+"F18.wireOp",EDGE,"E412"),sQuery(id+"F18.wireOp",EDGE,"E413"),sQuery(id+"F18.wireOp",EDGE,"E414"),sQuery(id+"F18.wireOp",EDGE,"E415"),sQuery(id+"F18.wireOp",EDGE,"E416"),sQuery(id+"F18.wireOp",EDGE,"E417"),sQuery(id+"F18.wireOp",EDGE,"E418"),sQuery(id+"F18.wireOp",EDGE,"E419"),sQuery(id+"F18.wireOp",EDGE,"E420"),sQuery(id+"F18.wireOp",EDGE,"E421"),sQuery(id+"F18.wireOp",EDGE,"E422"),sQuery(id+"F18.wireOp",EDGE,"E423"),sQuery(id+"F18.wireOp",EDGE,"E424")])]});
            var Q1;
            Q1=qCreatedBy(makeId("Origin.pointOp"),VERTEX);
            transform(context, id + "F20", {"entities" : qUnion([Q0]), "transformType" : TransformType.SCALE_UNIFORMLY, "scale" : 0.45, "scalePoint" : qUnion([Q1]), "makeCopy" : false});
        }
        {
            var Q0;
            Q0=makeQuery(id+"F19.opExtrude","SWEPT_BODY",BODY,{"disambiguationData":[OSD([sQuery(id+"F18.wireOp",EDGE,"E297"),sQuery(id+"F18.wireOp",EDGE,"E298"),sQuery(id+"F18.wireOp",EDGE,"E299"),sQuery(id+"F18.wireOp",EDGE,"E300"),sQuery(id+"F18.wireOp",EDGE,"E301"),sQuery(id+"F18.wireOp",EDGE,"E302"),sQuery(id+"F18.wireOp",EDGE,"E303"),sQuery(id+"F18.wireOp",EDGE,"E304"),sQuery(id+"F18.wireOp",EDGE,"E305"),sQuery(id+"F18.wireOp",EDGE,"E306"),sQuery(id+"F18.wireOp",EDGE,"E307"),sQuery(id+"F18.wireOp",EDGE,"E308"),sQuery(id+"F18.wireOp",EDGE,"E309"),sQuery(id+"F18.wireOp",EDGE,"E310"),sQuery(id+"F18.wireOp",EDGE,"E311"),sQuery(id+"F18.wireOp",EDGE,"E312"),sQuery(id+"F18.wireOp",EDGE,"E313"),sQuery(id+"F18.wireOp",EDGE,"E314"),sQuery(id+"F18.wireOp",EDGE,"E315"),sQuery(id+"F18.wireOp",EDGE,"E316"),sQuery(id+"F18.wireOp",EDGE,"E317"),sQuery(id+"F18.wireOp",EDGE,"E318"),sQuery(id+"F18.wireOp",EDGE,"E319"),sQuery(id+"F18.wireOp",EDGE,"E320"),sQuery(id+"F18.wireOp",EDGE,"E321"),sQuery(id+"F18.wireOp",EDGE,"E322"),sQuery(id+"F18.wireOp",EDGE,"E323"),sQuery(id+"F18.wireOp",EDGE,"E324"),sQuery(id+"F18.wireOp",EDGE,"E325"),sQuery(id+"F18.wireOp",EDGE,"E326"),sQuery(id+"F18.wireOp",EDGE,"E327"),sQuery(id+"F18.wireOp",EDGE,"E328"),sQuery(id+"F18.wireOp",EDGE,"E329"),sQuery(id+"F18.wireOp",EDGE,"E330"),sQuery(id+"F18.wireOp",EDGE,"E331"),sQuery(id+"F18.wireOp",EDGE,"E332"),sQuery(id+"F18.wireOp",EDGE,"E333"),sQuery(id+"F18.wireOp",EDGE,"E334"),sQuery(id+"F18.wireOp",EDGE,"E335"),sQuery(id+"F18.wireOp",EDGE,"E336"),sQuery(id+"F18.wireOp",EDGE,"E337"),sQuery(id+"F18.wireOp",EDGE,"E338"),sQuery(id+"F18.wireOp",EDGE,"E339"),sQuery(id+"F18.wireOp",EDGE,"E340"),sQuery(id+"F18.wireOp",EDGE,"E341"),sQuery(id+"F18.wireOp",EDGE,"E342"),sQuery(id+"F18.wireOp",EDGE,"E343"),sQuery(id+"F18.wireOp",EDGE,"E344"),sQuery(id+"F18.wireOp",EDGE,"E345"),sQuery(id+"F18.wireOp",EDGE,"E346"),sQuery(id+"F18.wireOp",EDGE,"E347"),sQuery(id+"F18.wireOp",EDGE,"E348"),sQuery(id+"F18.wireOp",EDGE,"E349"),sQuery(id+"F18.wireOp",EDGE,"E350"),sQuery(id+"F18.wireOp",EDGE,"E351"),sQuery(id+"F18.wireOp",EDGE,"E352"),sQuery(id+"F18.wireOp",EDGE,"E353"),sQuery(id+"F18.wireOp",EDGE,"E354"),sQuery(id+"F18.wireOp",EDGE,"E355"),sQuery(id+"F18.wireOp",EDGE,"E356"),sQuery(id+"F18.wireOp",EDGE,"E357"),sQuery(id+"F18.wireOp",EDGE,"E358"),sQuery(id+"F18.wireOp",EDGE,"E359"),sQuery(id+"F18.wireOp",EDGE,"E360"),sQuery(id+"F18.wireOp",EDGE,"E361"),sQuery(id+"F18.wireOp",EDGE,"E362"),sQuery(id+"F18.wireOp",EDGE,"E363"),sQuery(id+"F18.wireOp",EDGE,"E364"),sQuery(id+"F18.wireOp",EDGE,"E365"),sQuery(id+"F18.wireOp",EDGE,"E366"),sQuery(id+"F18.wireOp",EDGE,"E367"),sQuery(id+"F18.wireOp",EDGE,"E368"),sQuery(id+"F18.wireOp",EDGE,"E369"),sQuery(id+"F18.wireOp",EDGE,"E370"),sQuery(id+"F18.wireOp",EDGE,"E371"),sQuery(id+"F18.wireOp",EDGE,"E372"),sQuery(id+"F18.wireOp",EDGE,"E373"),sQuery(id+"F18.wireOp",EDGE,"E374"),sQuery(id+"F18.wireOp",EDGE,"E375"),sQuery(id+"F18.wireOp",EDGE,"E376"),sQuery(id+"F18.wireOp",EDGE,"E377"),sQuery(id+"F18.wireOp",EDGE,"E378"),sQuery(id+"F18.wireOp",EDGE,"E379"),sQuery(id+"F18.wireOp",EDGE,"E380"),sQuery(id+"F18.wireOp",EDGE,"E381"),sQuery(id+"F18.wireOp",EDGE,"E382"),sQuery(id+"F18.wireOp",EDGE,"E383"),sQuery(id+"F18.wireOp",EDGE,"E384"),sQuery(id+"F18.wireOp",EDGE,"E385"),sQuery(id+"F18.wireOp",EDGE,"E386"),sQuery(id+"F18.wireOp",EDGE,"E387"),sQuery(id+"F18.wireOp",EDGE,"E388"),sQuery(id+"F18.wireOp",EDGE,"E389"),sQuery(id+"F18.wireOp",EDGE,"E390"),sQuery(id+"F18.wireOp",EDGE,"E391"),sQuery(id+"F18.wireOp",EDGE,"E392"),sQuery(id+"F18.wireOp",EDGE,"E393"),sQuery(id+"F18.wireOp",EDGE,"E394"),sQuery(id+"F18.wireOp",EDGE,"E395"),sQuery(id+"F18.wireOp",EDGE,"E396"),sQuery(id+"F18.wireOp",EDGE,"E397"),sQuery(id+"F18.wireOp",EDGE,"E398"),sQuery(id+"F18.wireOp",EDGE,"E399"),sQuery(id+"F18.wireOp",EDGE,"E400"),sQuery(id+"F18.wireOp",EDGE,"E401"),sQuery(id+"F18.wireOp",EDGE,"E402"),sQuery(id+"F18.wireOp",EDGE,"E403"),sQuery(id+"F18.wireOp",EDGE,"E404"),sQuery(id+"F18.wireOp",EDGE,"E405"),sQuery(id+"F18.wireOp",EDGE,"E406"),sQuery(id+"F18.wireOp",EDGE,"E407"),sQuery(id+"F18.wireOp",EDGE,"E408"),sQuery(id+"F18.wireOp",EDGE,"E409"),sQuery(id+"F18.wireOp",EDGE,"E410"),sQuery(id+"F18.wireOp",EDGE,"E411"),sQuery(id+"F18.wireOp",EDGE,"E412"),sQuery(id+"F18.wireOp",EDGE,"E413"),sQuery(id+"F18.wireOp",EDGE,"E414"),sQuery(id+"F18.wireOp",EDGE,"E415"),sQuery(id+"F18.wireOp",EDGE,"E416"),sQuery(id+"F18.wireOp",EDGE,"E417"),sQuery(id+"F18.wireOp",EDGE,"E418"),sQuery(id+"F18.wireOp",EDGE,"E419"),sQuery(id+"F18.wireOp",EDGE,"E420"),sQuery(id+"F18.wireOp",EDGE,"E421"),sQuery(id+"F18.wireOp",EDGE,"E422"),sQuery(id+"F18.wireOp",EDGE,"E423"),sQuery(id+"F18.wireOp",EDGE,"E424")])]});
            transform(context, id + "F21", {"entities" : qUnion([Q0]), "transformType" : TransformType.TRANSLATION_3D, "dx" : 0 * mm, "dy" : -5 * mm, "dz" : 0 * mm, "makeCopy" : false});
        }
        {
            var Q0;
            Q0=makeQuery(id+"F12.opPattern","COPY",BODY,{"derivedFrom":makeQuery(id+"F6.opRevolve","SWEPT_BODY",BODY,{"disambiguationData":[OSD([sQuery(id+"F5.wireOp",EDGE,"E3"),sQuery(id+"F5.wireOp",EDGE,"E4"),sQuery(id+"F5.wireOp",EDGE,"E5")])]}),"instanceName":"1"});
            transform(context, id + "F22", {"entities" : qUnion([Q0]), "transformType" : TransformType.TRANSLATION_3D, "dx" : 0 * mm, "dy" : 0 * mm, "dz" : -1 * mm, "makeCopy" : false});
        }
        {
            var Q0;
            Q0=makeQuery(id+"F19.opExtrude","SWEPT_BODY",BODY,{"disambiguationData":[OSD([sQuery(id+"F18.wireOp",EDGE,"E297"),sQuery(id+"F18.wireOp",EDGE,"E298"),sQuery(id+"F18.wireOp",EDGE,"E299"),sQuery(id+"F18.wireOp",EDGE,"E300"),sQuery(id+"F18.wireOp",EDGE,"E301"),sQuery(id+"F18.wireOp",EDGE,"E302"),sQuery(id+"F18.wireOp",EDGE,"E303"),sQuery(id+"F18.wireOp",EDGE,"E304"),sQuery(id+"F18.wireOp",EDGE,"E305"),sQuery(id+"F18.wireOp",EDGE,"E306"),sQuery(id+"F18.wireOp",EDGE,"E307"),sQuery(id+"F18.wireOp",EDGE,"E308"),sQuery(id+"F18.wireOp",EDGE,"E309"),sQuery(id+"F18.wireOp",EDGE,"E310"),sQuery(id+"F18.wireOp",EDGE,"E311"),sQuery(id+"F18.wireOp",EDGE,"E312"),sQuery(id+"F18.wireOp",EDGE,"E313"),sQuery(id+"F18.wireOp",EDGE,"E314"),sQuery(id+"F18.wireOp",EDGE,"E315"),sQuery(id+"F18.wireOp",EDGE,"E316"),sQuery(id+"F18.wireOp",EDGE,"E317"),sQuery(id+"F18.wireOp",EDGE,"E318"),sQuery(id+"F18.wireOp",EDGE,"E319"),sQuery(id+"F18.wireOp",EDGE,"E320"),sQuery(id+"F18.wireOp",EDGE,"E321"),sQuery(id+"F18.wireOp",EDGE,"E322"),sQuery(id+"F18.wireOp",EDGE,"E323"),sQuery(id+"F18.wireOp",EDGE,"E324"),sQuery(id+"F18.wireOp",EDGE,"E325"),sQuery(id+"F18.wireOp",EDGE,"E326"),sQuery(id+"F18.wireOp",EDGE,"E327"),sQuery(id+"F18.wireOp",EDGE,"E328"),sQuery(id+"F18.wireOp",EDGE,"E329"),sQuery(id+"F18.wireOp",EDGE,"E330"),sQuery(id+"F18.wireOp",EDGE,"E331"),sQuery(id+"F18.wireOp",EDGE,"E332"),sQuery(id+"F18.wireOp",EDGE,"E333"),sQuery(id+"F18.wireOp",EDGE,"E334"),sQuery(id+"F18.wireOp",EDGE,"E335"),sQuery(id+"F18.wireOp",EDGE,"E336"),sQuery(id+"F18.wireOp",EDGE,"E337"),sQuery(id+"F18.wireOp",EDGE,"E338"),sQuery(id+"F18.wireOp",EDGE,"E339"),sQuery(id+"F18.wireOp",EDGE,"E340"),sQuery(id+"F18.wireOp",EDGE,"E341"),sQuery(id+"F18.wireOp",EDGE,"E342"),sQuery(id+"F18.wireOp",EDGE,"E343"),sQuery(id+"F18.wireOp",EDGE,"E344"),sQuery(id+"F18.wireOp",EDGE,"E345"),sQuery(id+"F18.wireOp",EDGE,"E346"),sQuery(id+"F18.wireOp",EDGE,"E347"),sQuery(id+"F18.wireOp",EDGE,"E348"),sQuery(id+"F18.wireOp",EDGE,"E349"),sQuery(id+"F18.wireOp",EDGE,"E350"),sQuery(id+"F18.wireOp",EDGE,"E351"),sQuery(id+"F18.wireOp",EDGE,"E352"),sQuery(id+"F18.wireOp",EDGE,"E353"),sQuery(id+"F18.wireOp",EDGE,"E354"),sQuery(id+"F18.wireOp",EDGE,"E355"),sQuery(id+"F18.wireOp",EDGE,"E356"),sQuery(id+"F18.wireOp",EDGE,"E357"),sQuery(id+"F18.wireOp",EDGE,"E358"),sQuery(id+"F18.wireOp",EDGE,"E359"),sQuery(id+"F18.wireOp",EDGE,"E360"),sQuery(id+"F18.wireOp",EDGE,"E361"),sQuery(id+"F18.wireOp",EDGE,"E362"),sQuery(id+"F18.wireOp",EDGE,"E363"),sQuery(id+"F18.wireOp",EDGE,"E364"),sQuery(id+"F18.wireOp",EDGE,"E365"),sQuery(id+"F18.wireOp",EDGE,"E366"),sQuery(id+"F18.wireOp",EDGE,"E367"),sQuery(id+"F18.wireOp",EDGE,"E368"),sQuery(id+"F18.wireOp",EDGE,"E369"),sQuery(id+"F18.wireOp",EDGE,"E370"),sQuery(id+"F18.wireOp",EDGE,"E371"),sQuery(id+"F18.wireOp",EDGE,"E372"),sQuery(id+"F18.wireOp",EDGE,"E373"),sQuery(id+"F18.wireOp",EDGE,"E374"),sQuery(id+"F18.wireOp",EDGE,"E375"),sQuery(id+"F18.wireOp",EDGE,"E376"),sQuery(id+"F18.wireOp",EDGE,"E377"),sQuery(id+"F18.wireOp",EDGE,"E378"),sQuery(id+"F18.wireOp",EDGE,"E379"),sQuery(id+"F18.wireOp",EDGE,"E380"),sQuery(id+"F18.wireOp",EDGE,"E381"),sQuery(id+"F18.wireOp",EDGE,"E382"),sQuery(id+"F18.wireOp",EDGE,"E383"),sQuery(id+"F18.wireOp",EDGE,"E384"),sQuery(id+"F18.wireOp",EDGE,"E385"),sQuery(id+"F18.wireOp",EDGE,"E386"),sQuery(id+"F18.wireOp",EDGE,"E387"),sQuery(id+"F18.wireOp",EDGE,"E388"),sQuery(id+"F18.wireOp",EDGE,"E389"),sQuery(id+"F18.wireOp",EDGE,"E390"),sQuery(id+"F18.wireOp",EDGE,"E391"),sQuery(id+"F18.wireOp",EDGE,"E392"),sQuery(id+"F18.wireOp",EDGE,"E393"),sQuery(id+"F18.wireOp",EDGE,"E394"),sQuery(id+"F18.wireOp",EDGE,"E395"),sQuery(id+"F18.wireOp",EDGE,"E396"),sQuery(id+"F18.wireOp",EDGE,"E397"),sQuery(id+"F18.wireOp",EDGE,"E398"),sQuery(id+"F18.wireOp",EDGE,"E399"),sQuery(id+"F18.wireOp",EDGE,"E400"),sQuery(id+"F18.wireOp",EDGE,"E401"),sQuery(id+"F18.wireOp",EDGE,"E402"),sQuery(id+"F18.wireOp",EDGE,"E403"),sQuery(id+"F18.wireOp",EDGE,"E404"),sQuery(id+"F18.wireOp",EDGE,"E405"),sQuery(id+"F18.wireOp",EDGE,"E406"),sQuery(id+"F18.wireOp",EDGE,"E407"),sQuery(id+"F18.wireOp",EDGE,"E408"),sQuery(id+"F18.wireOp",EDGE,"E409"),sQuery(id+"F18.wireOp",EDGE,"E410"),sQuery(id+"F18.wireOp",EDGE,"E411"),sQuery(id+"F18.wireOp",EDGE,"E412"),sQuery(id+"F18.wireOp",EDGE,"E413"),sQuery(id+"F18.wireOp",EDGE,"E414"),sQuery(id+"F18.wireOp",EDGE,"E415"),sQuery(id+"F18.wireOp",EDGE,"E416"),sQuery(id+"F18.wireOp",EDGE,"E417"),sQuery(id+"F18.wireOp",EDGE,"E418"),sQuery(id+"F18.wireOp",EDGE,"E419"),sQuery(id+"F18.wireOp",EDGE,"E420"),sQuery(id+"F18.wireOp",EDGE,"E421"),sQuery(id+"F18.wireOp",EDGE,"E422"),sQuery(id+"F18.wireOp",EDGE,"E423"),sQuery(id+"F18.wireOp",EDGE,"E424")])]});
            var Q1;
            Q1=makeQuery(id+"F12.opPattern","COPY",BODY,{"derivedFrom":makeQuery(id+"F6.opRevolve","SWEPT_BODY",BODY,{"disambiguationData":[OSD([sQuery(id+"F5.wireOp",EDGE,"E3"),sQuery(id+"F5.wireOp",EDGE,"E4"),sQuery(id+"F5.wireOp",EDGE,"E5")])]}),"instanceName":"1"});
            booleanBodies(context, id + "F23", {"operationType" : BooleanOperationType.INTERSECTION, "tools" : qUnion([Q0, Q1])});
        }
        {
            var Q0;
            Q0=makeQuery(id+"F23.opBoolean","INTERSECT",EDGE,{"derivedFrom":[makeQuery(id+"F12.opPattern","COPY",FACE,{"derivedFrom":makeQuery(id+"F6.opRevolve","SWEPT_FACE",FACE,{"disambiguationData":[OSD([sQuery(id+"F5.wireOp",EDGE,"E3")])]}),"instanceName":"1"}),makeQuery(id+"F19.opExtrude","SWEPT_FACE",FACE,{"disambiguationData":[OSD([sQuery(id+"F18.wireOp",EDGE,"E421")])]})]});
            fillet(context, id + "F24", {"entities" : qUnion([Q0]), "radius" : .3 * mm, "tangentPropagation" : true, "allowEdgeOverflow" : false});
        }
        {
            var Q0;
            Q0=qCreatedBy(makeId("Top.planeOp"),FACE);
            var sketch = newSketch(context, id + "F25", { "sketchPlane" : qUnion([Q0])});
            skLineSegment(sketch, "E425", {"start": v(-165.5, 847.5) * mm, "end": v(-165.5, 839) * mm});
            skLineSegment(sketch, "E426", {"start": v(-165.5, 839) * mm, "end": v(-347.5, 839) * mm});
            skLineSegment(sketch, "E427", {"start": v(-347.5, 839) * mm, "end": v(-529.5, 839) * mm});
            skLineSegment(sketch, "E428", {"start": v(-529.5, 839) * mm, "end": v(-529.5, 737.5) * mm});
            skLineSegment(sketch, "E429", {"start": v(-529.5, 737.5) * mm, "end": v(-529.5, 636) * mm});
            skLineSegment(sketch, "E430", {"start": v(-529.5, 636) * mm, "end": v(-347.5, 636) * mm});
            skLineSegment(sketch, "E431", {"start": v(-347.5, 636) * mm, "end": v(-165.5, 636) * mm});
            skLineSegment(sketch, "E432", {"start": v(-165.5, 636) * mm, "end": v(-165.5, 712.5) * mm});
            skLineSegment(sketch, "E433", {"start": v(-165.5, 712.5) * mm, "end": v(-165.5, 789) * mm});
            skLineSegment(sketch, "E434", {"start": v(-165.5, 789) * mm, "end": v(18.5, 789) * mm});
            skLineSegment(sketch, "E435", {"start": v(18.5, 789) * mm, "end": v(202.5, 789) * mm});
            skLineSegment(sketch, "E436", {"start": v(202.5, 789) * mm, "end": v(202.5, 712.5) * mm});
            skLineSegment(sketch, "E437", {"start": v(202.5, 712.5) * mm, "end": v(202.5, 636) * mm});
            skLineSegment(sketch, "E438", {"start": v(202.5, 636) * mm, "end": v(364.5, 636) * mm});
            skLineSegment(sketch, "E439", {"start": v(364.5, 636) * mm, "end": v(526.5, 636) * mm});
            skLineSegment(sketch, "E440", {"start": v(526.5, 636) * mm, "end": v(526.5, 733.5) * mm});
            skLineSegment(sketch, "E441", {"start": v(526.5, 733.5) * mm, "end": v(526.5, 831) * mm});
            skLineSegment(sketch, "E442", {"start": v(526.5, 831) * mm, "end": v(364.5, 831) * mm});
            skLineSegment(sketch, "E443", {"start": v(364.5, 831) * mm, "end": v(202.5, 831) * mm});
            skLineSegment(sketch, "E444", {"start": v(202.5, 831) * mm, "end": v(202.5, 843.5) * mm});
            skLineSegment(sketch, "E445", {"start": v(202.5, 843.5) * mm, "end": v(202.5, 856) * mm});
            skLineSegment(sketch, "E446", {"start": v(202.5, 856) * mm, "end": v(18.5, 856) * mm});
            skLineSegment(sketch, "E447", {"start": v(18.5, 856) * mm, "end": v(-165.5, 856) * mm});
            skLineSegment(sketch, "E448", {"start": v(-165.5, 856) * mm, "end": v(-165.5, 847.5) * mm});
            skLineSegment(sketch, "E449", {"start": v(-522.5, -741.5) * mm, "end": v(-522.5, -837) * mm});
            skLineSegment(sketch, "E450", {"start": v(-522.5, -837) * mm, "end": v(-344, -837) * mm});
            skLineSegment(sketch, "E451", {"start": v(-344, -837) * mm, "end": v(-165.5, -837) * mm});
            skLineSegment(sketch, "E452", {"start": v(-165.5, -837) * mm, "end": v(-165.5, -846.5) * mm});
            skLineSegment(sketch, "E453", {"start": v(-165.5, -846.5) * mm, "end": v(-165.5, -856) * mm});
            skLineSegment(sketch, "E454", {"start": v(-165.5, -856) * mm, "end": v(18.5, -856) * mm});
            skLineSegment(sketch, "E455", {"start": v(18.5, -856) * mm, "end": v(202.5, -856) * mm});
            skLineSegment(sketch, "E456", {"start": v(202.5, -856) * mm, "end": v(202.5, -843.5) * mm});
            skLineSegment(sketch, "E457", {"start": v(202.5, -843.5) * mm, "end": v(202.5, -831) * mm});
            skLineSegment(sketch, "E458", {"start": v(202.5, -831) * mm, "end": v(366, -831) * mm});
            skLineSegment(sketch, "E459", {"start": v(366, -831) * mm, "end": v(529.5, -831) * mm});
            skLineSegment(sketch, "E460", {"start": v(529.5, -831) * mm, "end": v(529.5, -739) * mm});
            skLineSegment(sketch, "E461", {"start": v(529.5, -739) * mm, "end": v(529.5, -647) * mm});
            skLineSegment(sketch, "E462", {"start": v(529.5, -647) * mm, "end": v(366, -647) * mm});
            skLineSegment(sketch, "E463", {"start": v(366, -647) * mm, "end": v(202.5, -647) * mm});
            skLineSegment(sketch, "E464", {"start": v(202.5, -647) * mm, "end": v(202.5, -718.5) * mm});
            skLineSegment(sketch, "E465", {"start": v(202.5, -718.5) * mm, "end": v(202.5, -790) * mm});
            skLineSegment(sketch, "E466", {"start": v(202.5, -790) * mm, "end": v(18.5, -790) * mm});
            skLineSegment(sketch, "E467", {"start": v(18.5, -790) * mm, "end": v(-165.5, -790) * mm});
            skLineSegment(sketch, "E468", {"start": v(-165.5, -790) * mm, "end": v(-165.5, -718) * mm});
            skLineSegment(sketch, "E469", {"start": v(-165.5, -718) * mm, "end": v(-165.5, -646) * mm});
            skLineSegment(sketch, "E470", {"start": v(-165.5, -646) * mm, "end": v(-344, -646) * mm});
            skLineSegment(sketch, "E471", {"start": v(-344, -646) * mm, "end": v(-522.5, -646) * mm});
            skLineSegment(sketch, "E472", {"start": v(-522.5, -646) * mm, "end": v(-522.5, -741.5) * mm});
            skSolve(sketch);
        }
        {
            var Q0;
            Q0 = qSketchRegion(id + "F25", true);
            extrude(context, id + "F26", {"entities" : qUnion([Q0]), "depth" : 150 * mm});
        }
        {
            var Q0;
            Q0=makeQuery(id+"F26.opExtrude","SWEPT_BODY",BODY,{"disambiguationData":[OSD([sQuery(id+"F25.wireOp",EDGE,"E449"),sQuery(id+"F25.wireOp",EDGE,"E450"),sQuery(id+"F25.wireOp",EDGE,"E451"),sQuery(id+"F25.wireOp",EDGE,"E452"),sQuery(id+"F25.wireOp",EDGE,"E453"),sQuery(id+"F25.wireOp",EDGE,"E454"),sQuery(id+"F25.wireOp",EDGE,"E455"),sQuery(id+"F25.wireOp",EDGE,"E456"),sQuery(id+"F25.wireOp",EDGE,"E457"),sQuery(id+"F25.wireOp",EDGE,"E458"),sQuery(id+"F25.wireOp",EDGE,"E459"),sQuery(id+"F25.wireOp",EDGE,"E460"),sQuery(id+"F25.wireOp",EDGE,"E461"),sQuery(id+"F25.wireOp",EDGE,"E462"),sQuery(id+"F25.wireOp",EDGE,"E463"),sQuery(id+"F25.wireOp",EDGE,"E464"),sQuery(id+"F25.wireOp",EDGE,"E465"),sQuery(id+"F25.wireOp",EDGE,"E466"),sQuery(id+"F25.wireOp",EDGE,"E467"),sQuery(id+"F25.wireOp",EDGE,"E468"),sQuery(id+"F25.wireOp",EDGE,"E469"),sQuery(id+"F25.wireOp",EDGE,"E470"),sQuery(id+"F25.wireOp",EDGE,"E471"),sQuery(id+"F25.wireOp",EDGE,"E472")])]});
            deleteBodies(context, id + "F27", {"entities" : qUnion([Q0])});
        }
        {
            var Q0;
            Q0=makeQuery(id+"F26.opExtrude","SWEPT_BODY",BODY,{"disambiguationData":[OSD([sQuery(id+"F25.wireOp",EDGE,"E425"),sQuery(id+"F25.wireOp",EDGE,"E426"),sQuery(id+"F25.wireOp",EDGE,"E427"),sQuery(id+"F25.wireOp",EDGE,"E428"),sQuery(id+"F25.wireOp",EDGE,"E429"),sQuery(id+"F25.wireOp",EDGE,"E430"),sQuery(id+"F25.wireOp",EDGE,"E431"),sQuery(id+"F25.wireOp",EDGE,"E432"),sQuery(id+"F25.wireOp",EDGE,"E433"),sQuery(id+"F25.wireOp",EDGE,"E434"),sQuery(id+"F25.wireOp",EDGE,"E435"),sQuery(id+"F25.wireOp",EDGE,"E436"),sQuery(id+"F25.wireOp",EDGE,"E437"),sQuery(id+"F25.wireOp",EDGE,"E438"),sQuery(id+"F25.wireOp",EDGE,"E439"),sQuery(id+"F25.wireOp",EDGE,"E440"),sQuery(id+"F25.wireOp",EDGE,"E441"),sQuery(id+"F25.wireOp",EDGE,"E442"),sQuery(id+"F25.wireOp",EDGE,"E443"),sQuery(id+"F25.wireOp",EDGE,"E444"),sQuery(id+"F25.wireOp",EDGE,"E445"),sQuery(id+"F25.wireOp",EDGE,"E446"),sQuery(id+"F25.wireOp",EDGE,"E447"),sQuery(id+"F25.wireOp",EDGE,"E448")])]});
            deleteBodies(context, id + "F28", {"entities" : qUnion([Q0])});
        }
        {
            var Q0;
            Q0=makeQuery(id+"F6.opRevolve","SWEPT_BODY",BODY,{"disambiguationData":[OSD([sQuery(id+"F5.wireOp",EDGE,"E3"),sQuery(id+"F5.wireOp",EDGE,"E4"),sQuery(id+"F5.wireOp",EDGE,"E5")])]});
            transform(context, id + "F29", {"entities" : qUnion([Q0]), "transformType" : TransformType.TRANSLATION_3D, "dx" : 0 * mm, "dy" : 0 * mm, "dz" : 0 * mm, "makeCopy" : true});
        }
        {
            var Q0;
            Q0=makeQuery(id+"F29.opPattern","COPY",BODY,{"derivedFrom":makeQuery(id+"F6.opRevolve","SWEPT_BODY",BODY,{"disambiguationData":[OSD([sQuery(id+"F5.wireOp",EDGE,"E3"),sQuery(id+"F5.wireOp",EDGE,"E4"),sQuery(id+"F5.wireOp",EDGE,"E5")])]}),"instanceName":"1"});
            transform(context, id + "F30", {"entities" : qUnion([Q0]), "transformType" : TransformType.TRANSLATION_3D, "dx" : 0 * mm, "dy" : 0 * mm, "dz" : -2 * mm, "makeCopy" : false});
        }
        {
            var Q0;
            Q0=makeQuery(id+"F29.opPattern","COPY",BODY,{"derivedFrom":makeQuery(id+"F6.opRevolve","SWEPT_BODY",BODY,{"disambiguationData":[OSD([sQuery(id+"F5.wireOp",EDGE,"E3"),sQuery(id+"F5.wireOp",EDGE,"E4"),sQuery(id+"F5.wireOp",EDGE,"E5")])]}),"instanceName":"1"});
            var Q1;
            Q1=makeQuery(id+"F9.opExtrude","SWEPT_BODY",BODY,{"disambiguationData":[OSD([sQuery(id+"F8.wireOp",EDGE,"E6"),sQuery(id+"F8.wireOp",EDGE,"E7"),sQuery(id+"F8.wireOp",EDGE,"E8"),sQuery(id+"F8.wireOp",EDGE,"E9"),sQuery(id+"F8.wireOp",EDGE,"E10"),sQuery(id+"F8.wireOp",EDGE,"E11"),sQuery(id+"F8.wireOp",EDGE,"E12"),sQuery(id+"F8.wireOp",EDGE,"E13"),sQuery(id+"F8.wireOp",EDGE,"E14"),sQuery(id+"F8.wireOp",EDGE,"E15"),sQuery(id+"F8.wireOp",EDGE,"E16"),sQuery(id+"F8.wireOp",EDGE,"E17"),sQuery(id+"F8.wireOp",EDGE,"E18"),sQuery(id+"F8.wireOp",EDGE,"E19"),sQuery(id+"F8.wireOp",EDGE,"E20"),sQuery(id+"F8.wireOp",EDGE,"E21"),sQuery(id+"F8.wireOp",EDGE,"E22"),sQuery(id+"F8.wireOp",EDGE,"E23"),sQuery(id+"F8.wireOp",EDGE,"E24"),sQuery(id+"F8.wireOp",EDGE,"E25"),sQuery(id+"F8.wireOp",EDGE,"E26"),sQuery(id+"F8.wireOp",EDGE,"E27"),sQuery(id+"F8.wireOp",EDGE,"E28"),sQuery(id+"F8.wireOp",EDGE,"E29"),sQuery(id+"F8.wireOp",EDGE,"E30"),sQuery(id+"F8.wireOp",EDGE,"E31"),sQuery(id+"F8.wireOp",EDGE,"E32"),sQuery(id+"F8.wireOp",EDGE,"E33"),sQuery(id+"F8.wireOp",EDGE,"E34"),sQuery(id+"F8.wireOp",EDGE,"E35"),sQuery(id+"F8.wireOp",EDGE,"E36"),sQuery(id+"F8.wireOp",EDGE,"E37"),sQuery(id+"F8.wireOp",EDGE,"E38"),sQuery(id+"F8.wireOp",EDGE,"E39"),sQuery(id+"F8.wireOp",EDGE,"E40"),sQuery(id+"F8.wireOp",EDGE,"E41"),sQuery(id+"F8.wireOp",EDGE,"E42"),sQuery(id+"F8.wireOp",EDGE,"E43"),sQuery(id+"F8.wireOp",EDGE,"E44"),sQuery(id+"F8.wireOp",EDGE,"E45"),sQuery(id+"F8.wireOp",EDGE,"E46"),sQuery(id+"F8.wireOp",EDGE,"E47"),sQuery(id+"F8.wireOp",EDGE,"E48"),sQuery(id+"F8.wireOp",EDGE,"E49"),sQuery(id+"F8.wireOp",EDGE,"E50"),sQuery(id+"F8.wireOp",EDGE,"E51"),sQuery(id+"F8.wireOp",EDGE,"E52"),sQuery(id+"F8.wireOp",EDGE,"E53"),sQuery(id+"F8.wireOp",EDGE,"E54"),sQuery(id+"F8.wireOp",EDGE,"E55"),sQuery(id+"F8.wireOp",EDGE,"E56"),sQuery(id+"F8.wireOp",EDGE,"E57"),sQuery(id+"F8.wireOp",EDGE,"E58"),sQuery(id+"F8.wireOp",EDGE,"E59"),sQuery(id+"F8.wireOp",EDGE,"E60"),sQuery(id+"F8.wireOp",EDGE,"E61"),sQuery(id+"F8.wireOp",EDGE,"E62"),sQuery(id+"F8.wireOp",EDGE,"E63"),sQuery(id+"F8.wireOp",EDGE,"E64"),sQuery(id+"F8.wireOp",EDGE,"E65"),sQuery(id+"F8.wireOp",EDGE,"E66"),sQuery(id+"F8.wireOp",EDGE,"E67"),sQuery(id+"F8.wireOp",EDGE,"E68"),sQuery(id+"F8.wireOp",EDGE,"E69"),sQuery(id+"F8.wireOp",EDGE,"E70"),sQuery(id+"F8.wireOp",EDGE,"E71"),sQuery(id+"F8.wireOp",EDGE,"E72"),sQuery(id+"F8.wireOp",EDGE,"E73"),sQuery(id+"F8.wireOp",EDGE,"E74"),sQuery(id+"F8.wireOp",EDGE,"E75"),sQuery(id+"F8.wireOp",EDGE,"E76"),sQuery(id+"F8.wireOp",EDGE,"E77"),sQuery(id+"F8.wireOp",EDGE,"E78"),sQuery(id+"F8.wireOp",EDGE,"E79"),sQuery(id+"F8.wireOp",EDGE,"E80"),sQuery(id+"F8.wireOp",EDGE,"E81"),sQuery(id+"F8.wireOp",EDGE,"E82"),sQuery(id+"F8.wireOp",EDGE,"E83"),sQuery(id+"F8.wireOp",EDGE,"E84"),sQuery(id+"F8.wireOp",EDGE,"E85"),sQuery(id+"F8.wireOp",EDGE,"E86"),sQuery(id+"F8.wireOp",EDGE,"E87"),sQuery(id+"F8.wireOp",EDGE,"E88"),sQuery(id+"F8.wireOp",EDGE,"E89"),sQuery(id+"F8.wireOp",EDGE,"E90"),sQuery(id+"F8.wireOp",EDGE,"E91"),sQuery(id+"F8.wireOp",EDGE,"E92"),sQuery(id+"F8.wireOp",EDGE,"E93"),sQuery(id+"F8.wireOp",EDGE,"E94"),sQuery(id+"F8.wireOp",EDGE,"E95"),sQuery(id+"F8.wireOp",EDGE,"E96"),sQuery(id+"F8.wireOp",EDGE,"E97"),sQuery(id+"F8.wireOp",EDGE,"E98"),sQuery(id+"F8.wireOp",EDGE,"E99"),sQuery(id+"F8.wireOp",EDGE,"E100"),sQuery(id+"F8.wireOp",EDGE,"E101"),sQuery(id+"F8.wireOp",EDGE,"E102"),sQuery(id+"F8.wireOp",EDGE,"E103"),sQuery(id+"F8.wireOp",EDGE,"E104"),sQuery(id+"F8.wireOp",EDGE,"E105"),sQuery(id+"F8.wireOp",EDGE,"E106"),sQuery(id+"F8.wireOp",EDGE,"E107"),sQuery(id+"F8.wireOp",EDGE,"E108"),sQuery(id+"F8.wireOp",EDGE,"E109"),sQuery(id+"F8.wireOp",EDGE,"E110"),sQuery(id+"F8.wireOp",EDGE,"E111"),sQuery(id+"F8.wireOp",EDGE,"E112"),sQuery(id+"F8.wireOp",EDGE,"E113"),sQuery(id+"F8.wireOp",EDGE,"E114"),sQuery(id+"F8.wireOp",EDGE,"E115"),sQuery(id+"F8.wireOp",EDGE,"E116"),sQuery(id+"F8.wireOp",EDGE,"E117"),sQuery(id+"F8.wireOp",EDGE,"E118"),sQuery(id+"F8.wireOp",EDGE,"E119"),sQuery(id+"F8.wireOp",EDGE,"E120"),sQuery(id+"F8.wireOp",EDGE,"E121"),sQuery(id+"F8.wireOp",EDGE,"E122"),sQuery(id+"F8.wireOp",EDGE,"E123"),sQuery(id+"F8.wireOp",EDGE,"E124"),sQuery(id+"F8.wireOp",EDGE,"E125"),sQuery(id+"F8.wireOp",EDGE,"E126"),sQuery(id+"F8.wireOp",EDGE,"E127"),sQuery(id+"F8.wireOp",EDGE,"E128"),sQuery(id+"F8.wireOp",EDGE,"E129"),sQuery(id+"F8.wireOp",EDGE,"E130"),sQuery(id+"F8.wireOp",EDGE,"E131"),sQuery(id+"F8.wireOp",EDGE,"E132"),sQuery(id+"F8.wireOp",EDGE,"E133"),sQuery(id+"F8.wireOp",EDGE,"E134"),sQuery(id+"F8.wireOp",EDGE,"E135"),sQuery(id+"F8.wireOp",EDGE,"E136"),sQuery(id+"F8.wireOp",EDGE,"E137"),sQuery(id+"F8.wireOp",EDGE,"E138"),sQuery(id+"F8.wireOp",EDGE,"E139"),sQuery(id+"F8.wireOp",EDGE,"E140"),sQuery(id+"F8.wireOp",EDGE,"E141"),sQuery(id+"F8.wireOp",EDGE,"E142"),sQuery(id+"F8.wireOp",EDGE,"E143"),sQuery(id+"F8.wireOp",EDGE,"E144"),sQuery(id+"F8.wireOp",EDGE,"E145"),sQuery(id+"F8.wireOp",EDGE,"E146"),sQuery(id+"F8.wireOp",EDGE,"E147"),sQuery(id+"F8.wireOp",EDGE,"E148"),sQuery(id+"F8.wireOp",EDGE,"E149"),sQuery(id+"F8.wireOp",EDGE,"E150"),sQuery(id+"F8.wireOp",EDGE,"E151"),sQuery(id+"F8.wireOp",EDGE,"E152"),sQuery(id+"F8.wireOp",EDGE,"E153"),sQuery(id+"F8.wireOp",EDGE,"E154"),sQuery(id+"F8.wireOp",EDGE,"E155"),sQuery(id+"F8.wireOp",EDGE,"E156"),sQuery(id+"F8.wireOp",EDGE,"E157"),sQuery(id+"F8.wireOp",EDGE,"E158"),sQuery(id+"F8.wireOp",EDGE,"E159"),sQuery(id+"F8.wireOp",EDGE,"E160"),sQuery(id+"F8.wireOp",EDGE,"E161"),sQuery(id+"F8.wireOp",EDGE,"E162"),sQuery(id+"F8.wireOp",EDGE,"E163"),sQuery(id+"F8.wireOp",EDGE,"E164"),sQuery(id+"F8.wireOp",EDGE,"E165"),sQuery(id+"F8.wireOp",EDGE,"E166"),sQuery(id+"F8.wireOp",EDGE,"E167"),sQuery(id+"F8.wireOp",EDGE,"E168"),sQuery(id+"F8.wireOp",EDGE,"E169"),sQuery(id+"F8.wireOp",EDGE,"E170"),sQuery(id+"F8.wireOp",EDGE,"E171"),sQuery(id+"F8.wireOp",EDGE,"E172"),sQuery(id+"F8.wireOp",EDGE,"E173"),sQuery(id+"F8.wireOp",EDGE,"E174"),sQuery(id+"F8.wireOp",EDGE,"E175"),sQuery(id+"F8.wireOp",EDGE,"E176"),sQuery(id+"F8.wireOp",EDGE,"E177"),sQuery(id+"F8.wireOp",EDGE,"E178"),sQuery(id+"F8.wireOp",EDGE,"E179"),sQuery(id+"F8.wireOp",EDGE,"E180"),sQuery(id+"F8.wireOp",EDGE,"E181"),sQuery(id+"F8.wireOp",EDGE,"E182"),sQuery(id+"F8.wireOp",EDGE,"E183"),sQuery(id+"F8.wireOp",EDGE,"E184"),sQuery(id+"F8.wireOp",EDGE,"E185"),sQuery(id+"F8.wireOp",EDGE,"E186"),sQuery(id+"F8.wireOp",EDGE,"E187"),sQuery(id+"F8.wireOp",EDGE,"E188"),sQuery(id+"F8.wireOp",EDGE,"E189"),sQuery(id+"F8.wireOp",EDGE,"E190"),sQuery(id+"F8.wireOp",EDGE,"E191"),sQuery(id+"F8.wireOp",EDGE,"E192"),sQuery(id+"F8.wireOp",EDGE,"E193"),sQuery(id+"F8.wireOp",EDGE,"E194"),sQuery(id+"F8.wireOp",EDGE,"E195"),sQuery(id+"F8.wireOp",EDGE,"E196"),sQuery(id+"F8.wireOp",EDGE,"E197"),sQuery(id+"F8.wireOp",EDGE,"E198"),sQuery(id+"F8.wireOp",EDGE,"E199"),sQuery(id+"F8.wireOp",EDGE,"E200"),sQuery(id+"F8.wireOp",EDGE,"E201"),sQuery(id+"F8.wireOp",EDGE,"E202"),sQuery(id+"F8.wireOp",EDGE,"E203"),sQuery(id+"F8.wireOp",EDGE,"E204"),sQuery(id+"F8.wireOp",EDGE,"E205"),sQuery(id+"F8.wireOp",EDGE,"E206"),sQuery(id+"F8.wireOp",EDGE,"E207"),sQuery(id+"F8.wireOp",EDGE,"E208"),sQuery(id+"F8.wireOp",EDGE,"E209"),sQuery(id+"F8.wireOp",EDGE,"E210"),sQuery(id+"F8.wireOp",EDGE,"E211"),sQuery(id+"F8.wireOp",EDGE,"E212"),sQuery(id+"F8.wireOp",EDGE,"E213"),sQuery(id+"F8.wireOp",EDGE,"E214"),sQuery(id+"F8.wireOp",EDGE,"E215"),sQuery(id+"F8.wireOp",EDGE,"E216"),sQuery(id+"F8.wireOp",EDGE,"E217"),sQuery(id+"F8.wireOp",EDGE,"E218"),sQuery(id+"F8.wireOp",EDGE,"E219"),sQuery(id+"F8.wireOp",EDGE,"E220"),sQuery(id+"F8.wireOp",EDGE,"E221"),sQuery(id+"F8.wireOp",EDGE,"E222"),sQuery(id+"F8.wireOp",EDGE,"E223"),sQuery(id+"F8.wireOp",EDGE,"E224"),sQuery(id+"F8.wireOp",EDGE,"E225"),sQuery(id+"F8.wireOp",EDGE,"E226"),sQuery(id+"F8.wireOp",EDGE,"E227"),sQuery(id+"F8.wireOp",EDGE,"E228"),sQuery(id+"F8.wireOp",EDGE,"E229"),sQuery(id+"F8.wireOp",EDGE,"E230"),sQuery(id+"F8.wireOp",EDGE,"E231"),sQuery(id+"F8.wireOp",EDGE,"E232"),sQuery(id+"F8.wireOp",EDGE,"E233"),sQuery(id+"F8.wireOp",EDGE,"E234"),sQuery(id+"F8.wireOp",EDGE,"E235"),sQuery(id+"F8.wireOp",EDGE,"E236"),sQuery(id+"F8.wireOp",EDGE,"E237"),sQuery(id+"F8.wireOp",EDGE,"E238"),sQuery(id+"F8.wireOp",EDGE,"E239"),sQuery(id+"F8.wireOp",EDGE,"E240"),sQuery(id+"F8.wireOp",EDGE,"E241"),sQuery(id+"F8.wireOp",EDGE,"E242"),sQuery(id+"F8.wireOp",EDGE,"E243"),sQuery(id+"F8.wireOp",EDGE,"E244"),sQuery(id+"F8.wireOp",EDGE,"E245"),sQuery(id+"F8.wireOp",EDGE,"E246"),sQuery(id+"F8.wireOp",EDGE,"E247"),sQuery(id+"F8.wireOp",EDGE,"E248"),sQuery(id+"F8.wireOp",EDGE,"E249"),sQuery(id+"F8.wireOp",EDGE,"E250"),sQuery(id+"F8.wireOp",EDGE,"E251"),sQuery(id+"F8.wireOp",EDGE,"E252"),sQuery(id+"F8.wireOp",EDGE,"E253"),sQuery(id+"F8.wireOp",EDGE,"E254"),sQuery(id+"F8.wireOp",EDGE,"E255"),sQuery(id+"F8.wireOp",EDGE,"E256"),sQuery(id+"F8.wireOp",EDGE,"E257"),sQuery(id+"F8.wireOp",EDGE,"E258"),sQuery(id+"F8.wireOp",EDGE,"E259"),sQuery(id+"F8.wireOp",EDGE,"E260"),sQuery(id+"F8.wireOp",EDGE,"E261"),sQuery(id+"F8.wireOp",EDGE,"E262"),sQuery(id+"F8.wireOp",EDGE,"E263"),sQuery(id+"F8.wireOp",EDGE,"E264"),sQuery(id+"F8.wireOp",EDGE,"E265"),sQuery(id+"F8.wireOp",EDGE,"E266"),sQuery(id+"F8.wireOp",EDGE,"E267"),sQuery(id+"F8.wireOp",EDGE,"E268"),sQuery(id+"F8.wireOp",EDGE,"E269"),sQuery(id+"F8.wireOp",EDGE,"E270"),sQuery(id+"F8.wireOp",EDGE,"E271"),sQuery(id+"F8.wireOp",EDGE,"E272"),sQuery(id+"F8.wireOp",EDGE,"E273"),sQuery(id+"F8.wireOp",EDGE,"E274"),sQuery(id+"F8.wireOp",EDGE,"E275"),sQuery(id+"F8.wireOp",EDGE,"E276"),sQuery(id+"F8.wireOp",EDGE,"E277"),sQuery(id+"F8.wireOp",EDGE,"E278"),sQuery(id+"F8.wireOp",EDGE,"E279"),sQuery(id+"F8.wireOp",EDGE,"E280"),sQuery(id+"F8.wireOp",EDGE,"E281"),sQuery(id+"F8.wireOp",EDGE,"E282"),sQuery(id+"F8.wireOp",EDGE,"E283"),sQuery(id+"F8.wireOp",EDGE,"E284"),sQuery(id+"F8.wireOp",EDGE,"E285"),sQuery(id+"F8.wireOp",EDGE,"E286"),sQuery(id+"F8.wireOp",EDGE,"E287"),sQuery(id+"F8.wireOp",EDGE,"E288"),sQuery(id+"F8.wireOp",EDGE,"E289"),sQuery(id+"F8.wireOp",EDGE,"E290"),sQuery(id+"F8.wireOp",EDGE,"E291"),sQuery(id+"F8.wireOp",EDGE,"E292"),sQuery(id+"F8.wireOp",EDGE,"E293"),sQuery(id+"F8.wireOp",EDGE,"E294"),sQuery(id+"F8.wireOp",EDGE,"E295")])]});
            booleanBodies(context, id + "F31", {"operationType" : BooleanOperationType.INTERSECTION, "tools" : qUnion([Q0, Q1]), "keepTools" : true});
        }
        {
            var Q0;
            Q0=makeQuery(id+"F17.opBoolean","INTERSECT",BODY,{"derivedFrom":[makeQuery(id+"F13.opPattern","COPY",BODY,{"derivedFrom":makeQuery(id+"F12.opPattern","COPY",BODY,{"derivedFrom":makeQuery(id+"F6.opRevolve","SWEPT_BODY",BODY,{"disambiguationData":[OSD([sQuery(id+"F5.wireOp",EDGE,"E3"),sQuery(id+"F5.wireOp",EDGE,"E4"),sQuery(id+"F5.wireOp",EDGE,"E5")])]}),"instanceName":"1"}),"instanceName":"1"}),makeQuery(id+"F16.opExtrude","SWEPT_BODY",BODY,{"disambiguationData":[OSD([sQuery(id+"F15.wireOp",EDGE,"E296")])]})]});
            deleteBodies(context, id + "F32", {"entities" : qUnion([Q0])});
        }
        {
            var Q0;
            Q0=qCreatedBy(makeId("Top.planeOp"),FACE);
            var sketch = newSketch(context, id + "F33", { "sketchPlane" : qUnion([Q0])});
            skCircle(sketch, "E473", {"center": v(0, 0) * mm, "radius": 28 * mm});
            skSolve(sketch);
        }
        {
            var Q0;
            Q0 = qSketchRegion(id + "F33", true);
            extrude(context, id + "F34", {"entities" : qUnion([Q0]), "depth" : 25 * mm});
        }
        {
            var Q0;
            Q0=makeQuery(id+"F34.opExtrude","SWEPT_BODY",BODY,{"disambiguationData":[OSD([sQuery(id+"F33.wireOp",EDGE,"E473")])]});
            var Q1;
            Q1=makeQuery(id+"F6.opRevolve","SWEPT_BODY",BODY,{"disambiguationData":[OSD([sQuery(id+"F5.wireOp",EDGE,"E3"),sQuery(id+"F5.wireOp",EDGE,"E4"),sQuery(id+"F5.wireOp",EDGE,"E5")])]});
            booleanBodies(context, id + "F35", {"operationType" : BooleanOperationType.INTERSECTION, "tools" : qUnion([Q0, Q1]), "keepTools" : true});
        }
        {
            var Q0;
            Q0=makeQuery(id+"F35.opBoolean","INTERSECT",BODY,{"derivedFrom":[makeQuery(id+"F6.opRevolve","SWEPT_BODY",BODY,{"disambiguationData":[OSD([sQuery(id+"F5.wireOp",EDGE,"E3"),sQuery(id+"F5.wireOp",EDGE,"E4"),sQuery(id+"F5.wireOp",EDGE,"E5")])]}),makeQuery(id+"F34.opExtrude","SWEPT_BODY",BODY,{"disambiguationData":[OSD([sQuery(id+"F33.wireOp",EDGE,"E473")])]})]});
            transform(context, id + "F36", {"entities" : qUnion([Q0]), "transformType" : TransformType.TRANSLATION_3D, "dx" : 0 * mm, "dy" : 0 * mm, "dz" : -3.5 * mm, "makeCopy" : false});
        }
        {
            var Q0;
            Q0=qCreatedBy(makeId("Top.planeOp"),FACE);
            var sketch = newSketch(context, id + "F37", { "sketchPlane" : qUnion([Q0])});
            skLineSegment(sketch, "E474.bottom", {"start": v(56.64, -45.9) * mm, "end": v(-56.64, -45.9) * mm});
            skLineSegment(sketch, "E474.top", {"start": v(56.64, 45.9) * mm, "end": v(-56.64, 45.9) * mm});
            skLineSegment(sketch, "E474.left", {"start": v(56.64, -45.9) * mm, "end": v(56.64, 45.9) * mm});
            skLineSegment(sketch, "E474.right", {"start": v(-56.64, -45.9) * mm, "end": v(-56.64, 45.9) * mm});
            skPoint(sketch, "E474.middle", {"position": v(0, 0) * mm});
            skSolve(sketch);
        }
        {
            var Q0;
            Q0 = qSketchRegion(id + "F37", true);
            extrude(context, id + "F38", {"entities" : qUnion([Q0]), "depth" : -10 * mm});
        }
        {
            var Q0;
            Q0=makeQuery(id+"F38.opExtrude","SWEPT_BODY",BODY,{"disambiguationData":[OSD([sQuery(id+"F37.wireOp",EDGE,"E474.bottom"),sQuery(id+"F37.wireOp",EDGE,"E474.top"),sQuery(id+"F37.wireOp",EDGE,"E474.left"),sQuery(id+"F37.wireOp",EDGE,"E474.right")])]});
            var Q1;
            Q1=makeQuery(id+"F35.opBoolean","INTERSECT",BODY,{"derivedFrom":[makeQuery(id+"F6.opRevolve","SWEPT_BODY",BODY,{"disambiguationData":[OSD([sQuery(id+"F5.wireOp",EDGE,"E3"),sQuery(id+"F5.wireOp",EDGE,"E4"),sQuery(id+"F5.wireOp",EDGE,"E5")])]}),makeQuery(id+"F34.opExtrude","SWEPT_BODY",BODY,{"disambiguationData":[OSD([sQuery(id+"F33.wireOp",EDGE,"E473")])]})]});
            booleanBodies(context, id + "F39", {"operationType" : BooleanOperationType.SUBTRACTION, "tools" : qUnion([Q0]), "targets" : qUnion([Q1])});
        }
    });
